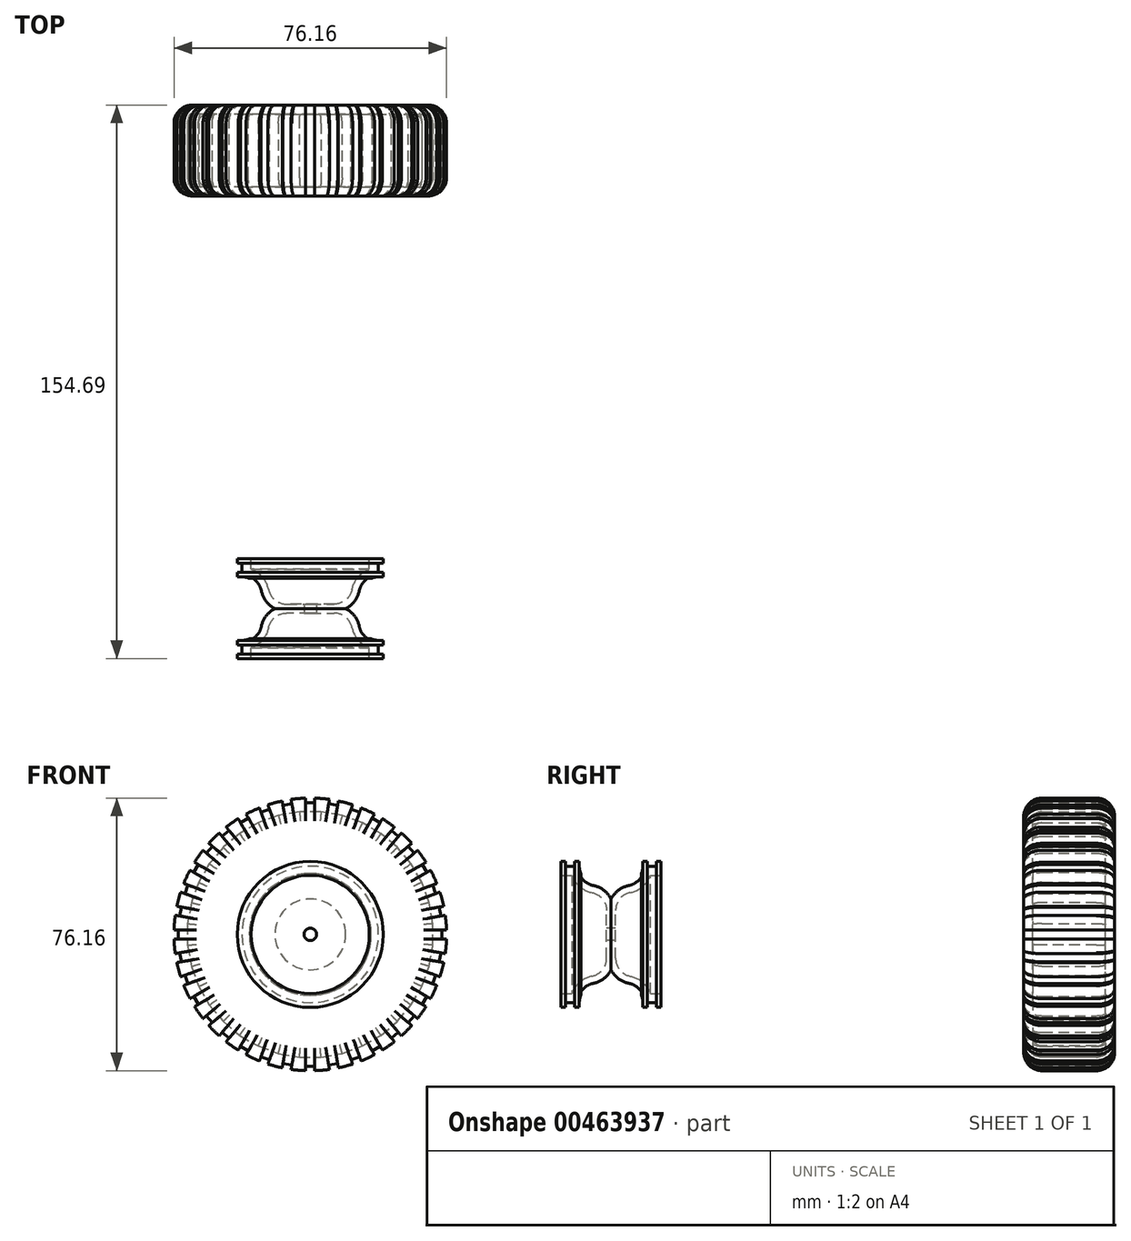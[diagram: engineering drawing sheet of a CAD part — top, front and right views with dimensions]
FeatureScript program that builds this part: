
annotation { "Feature Type Name" : "Feature", "Feature Type Description" : "" }
export const myFeature = defineFeature(function(context is Context, id is Id, definition is map)
    precondition{}
    {
        {
            var Q0;
            Q0=qCreatedBy(makeId("Front.planeOp"),FACE);
            var sketch = newSketch(context, id + "F0", { "sketchPlane" : qUnion([Q0])});
            skArc(sketch, "E0", {"start": v(-1.27, 38.08) * mm, "mid": v(-3.32, 37.96) * mm, "end": v(-5.36, 37.72) * mm});
            skCircle(sketch, "E1", {"center": v(0, 0) * mm, "radius": 19.05 * mm});
            skLineSegment(sketch, "E2.bottom", {"start": v(1.27, 36.83) * mm, "end": v(-1.27, 36.83) * mm});
            skLineSegment(sketch, "E2.left", {"start": v(1.27, 36.83) * mm, "end": v(1.27, 38.08) * mm});
            skLineSegment(sketch, "E2.right", {"start": v(-1.27, 36.83) * mm, "end": v(-1.27, 38.08) * mm});
            skPoint(sketch, "E2.middle", {"position": v(0, 38.1) * mm});
            skPoint(sketch, "E3.orphan", {"position": v(-1.27, 39.37) * mm});
            skPoint(sketch, "E4.orphan", {"position": v(1.27, 39.37) * mm});
            skPoint(sketch, "E5.1.0", {"position": v(8.09, 38.55) * mm});
            skPoint(sketch, "E5.1.1", {"position": v(5.59, 39) * mm});
            skPoint(sketch, "E5.1.2", {"position": v(6.62, 37.52) * mm});
            skLineSegment(sketch, "E5.1.3", {"start": v(5.14, 36.5) * mm, "end": v(5.36, 37.72) * mm});
            skLineSegment(sketch, "E5.1.4", {"start": v(7.65, 36.05) * mm, "end": v(7.86, 37.28) * mm});
            skLineSegment(sketch, "E5.1.5", {"start": v(7.65, 36.05) * mm, "end": v(5.14, 36.5) * mm});
            skPoint(sketch, "E5.2.0", {"position": v(14.66, 36.56) * mm});
            skPoint(sketch, "E5.2.1", {"position": v(12.27, 37.43) * mm});
            skPoint(sketch, "E5.2.2", {"position": v(13.03, 35.8) * mm});
            skLineSegment(sketch, "E5.2.3", {"start": v(11.4, 35.04) * mm, "end": v(11.83, 36.22) * mm});
            skLineSegment(sketch, "E5.2.4", {"start": v(13.8, 34.17) * mm, "end": v(14.22, 35.35) * mm});
            skLineSegment(sketch, "E5.2.5", {"start": v(13.8, 34.17) * mm, "end": v(11.4, 35.04) * mm});
            skPoint(sketch, "E5.3.0", {"position": v(20.78, 33.46) * mm});
            skPoint(sketch, "E5.3.1", {"position": v(18.59, 34.73) * mm});
            skPoint(sketch, "E5.3.2", {"position": v(19.05, 33) * mm});
            skLineSegment(sketch, "E5.3.3", {"start": v(17.32, 32.53) * mm, "end": v(17.94, 33.61) * mm});
            skLineSegment(sketch, "E5.3.4", {"start": v(19.51, 31.26) * mm, "end": v(20.14, 32.34) * mm});
            skLineSegment(sketch, "E5.3.5", {"start": v(19.51, 31.26) * mm, "end": v(17.32, 32.53) * mm});
            skPoint(sketch, "E5.4.0", {"position": v(26.28, 29.34) * mm});
            skPoint(sketch, "E5.4.1", {"position": v(24.33, 30.98) * mm});
            skPoint(sketch, "E5.4.2", {"position": v(24.5, 29.19) * mm});
            skLineSegment(sketch, "E5.4.3", {"start": v(22.7, 29.03) * mm, "end": v(23.5, 29.99) * mm});
            skLineSegment(sketch, "E5.4.4", {"start": v(24.65, 27.4) * mm, "end": v(25.45, 28.35) * mm});
            skLineSegment(sketch, "E5.4.5", {"start": v(24.65, 27.4) * mm, "end": v(22.7, 29.03) * mm});
            skPoint(sketch, "E5.5.0", {"position": v(30.98, 24.33) * mm});
            skPoint(sketch, "E5.5.1", {"position": v(29.34, 26.28) * mm});
            skPoint(sketch, "E5.5.2", {"position": v(29.19, 24.5) * mm});
            skLineSegment(sketch, "E5.5.3", {"start": v(27.4, 24.65) * mm, "end": v(28.35, 25.45) * mm});
            skLineSegment(sketch, "E5.5.4", {"start": v(29.03, 22.7) * mm, "end": v(29.99, 23.5) * mm});
            skLineSegment(sketch, "E5.5.5", {"start": v(29.03, 22.7) * mm, "end": v(27.4, 24.65) * mm});
            skPoint(sketch, "E5.6.0", {"position": v(34.73, 18.59) * mm});
            skPoint(sketch, "E5.6.1", {"position": v(33.46, 20.78) * mm});
            skPoint(sketch, "E5.6.2", {"position": v(33, 19.05) * mm});
            skLineSegment(sketch, "E5.6.3", {"start": v(31.26, 19.51) * mm, "end": v(32.34, 20.14) * mm});
            skLineSegment(sketch, "E5.6.4", {"start": v(32.53, 17.32) * mm, "end": v(33.61, 17.94) * mm});
            skLineSegment(sketch, "E5.6.5", {"start": v(32.53, 17.32) * mm, "end": v(31.26, 19.51) * mm});
            skPoint(sketch, "E5.7.0", {"position": v(37.43, 12.27) * mm});
            skPoint(sketch, "E5.7.1", {"position": v(36.56, 14.66) * mm});
            skPoint(sketch, "E5.7.2", {"position": v(35.8, 13.03) * mm});
            skLineSegment(sketch, "E5.7.3", {"start": v(34.17, 13.8) * mm, "end": v(35.35, 14.22) * mm});
            skLineSegment(sketch, "E5.7.4", {"start": v(35.04, 11.4) * mm, "end": v(36.22, 11.83) * mm});
            skLineSegment(sketch, "E5.7.5", {"start": v(35.04, 11.4) * mm, "end": v(34.17, 13.8) * mm});
            skPoint(sketch, "E5.8.0", {"position": v(39, 5.59) * mm});
            skPoint(sketch, "E5.8.1", {"position": v(38.55, 8.09) * mm});
            skPoint(sketch, "E5.8.2", {"position": v(37.52, 6.62) * mm});
            skLineSegment(sketch, "E5.8.3", {"start": v(36.05, 7.65) * mm, "end": v(37.28, 7.86) * mm});
            skLineSegment(sketch, "E5.8.4", {"start": v(36.5, 5.14) * mm, "end": v(37.72, 5.36) * mm});
            skLineSegment(sketch, "E5.8.5", {"start": v(36.5, 5.14) * mm, "end": v(36.05, 7.65) * mm});
            skPoint(sketch, "E5.9.0", {"position": v(39.37, -1.27) * mm});
            skPoint(sketch, "E5.9.1", {"position": v(39.37, 1.27) * mm});
            skPoint(sketch, "E5.9.2", {"position": v(38.1, 0) * mm});
            skLineSegment(sketch, "E5.9.3", {"start": v(36.83, 1.27) * mm, "end": v(38.08, 1.27) * mm});
            skLineSegment(sketch, "E5.9.4", {"start": v(36.83, -1.27) * mm, "end": v(38.08, -1.27) * mm});
            skLineSegment(sketch, "E5.9.5", {"start": v(36.83, -1.27) * mm, "end": v(36.83, 1.27) * mm});
            skPoint(sketch, "E5.10.0", {"position": v(38.55, -8.09) * mm});
            skPoint(sketch, "E5.10.1", {"position": v(39, -5.59) * mm});
            skPoint(sketch, "E5.10.2", {"position": v(37.52, -6.62) * mm});
            skLineSegment(sketch, "E5.10.3", {"start": v(36.5, -5.14) * mm, "end": v(37.72, -5.36) * mm});
            skLineSegment(sketch, "E5.10.4", {"start": v(36.05, -7.65) * mm, "end": v(37.28, -7.86) * mm});
            skLineSegment(sketch, "E5.10.5", {"start": v(36.05, -7.65) * mm, "end": v(36.5, -5.14) * mm});
            skPoint(sketch, "E5.11.0", {"position": v(36.56, -14.66) * mm});
            skPoint(sketch, "E5.11.1", {"position": v(37.43, -12.27) * mm});
            skPoint(sketch, "E5.11.2", {"position": v(35.8, -13.03) * mm});
            skLineSegment(sketch, "E5.11.3", {"start": v(35.04, -11.4) * mm, "end": v(36.22, -11.83) * mm});
            skLineSegment(sketch, "E5.11.4", {"start": v(34.17, -13.8) * mm, "end": v(35.35, -14.22) * mm});
            skLineSegment(sketch, "E5.11.5", {"start": v(34.17, -13.8) * mm, "end": v(35.04, -11.4) * mm});
            skPoint(sketch, "E5.12.0", {"position": v(33.46, -20.78) * mm});
            skPoint(sketch, "E5.12.1", {"position": v(34.73, -18.59) * mm});
            skPoint(sketch, "E5.12.2", {"position": v(33, -19.05) * mm});
            skLineSegment(sketch, "E5.12.3", {"start": v(32.53, -17.32) * mm, "end": v(33.61, -17.94) * mm});
            skLineSegment(sketch, "E5.12.4", {"start": v(31.26, -19.51) * mm, "end": v(32.34, -20.14) * mm});
            skLineSegment(sketch, "E5.12.5", {"start": v(31.26, -19.51) * mm, "end": v(32.53, -17.32) * mm});
            skPoint(sketch, "E5.13.0", {"position": v(29.34, -26.28) * mm});
            skPoint(sketch, "E5.13.1", {"position": v(30.98, -24.33) * mm});
            skPoint(sketch, "E5.13.2", {"position": v(29.19, -24.5) * mm});
            skLineSegment(sketch, "E5.13.3", {"start": v(29.03, -22.7) * mm, "end": v(29.99, -23.5) * mm});
            skLineSegment(sketch, "E5.13.4", {"start": v(27.4, -24.65) * mm, "end": v(28.35, -25.45) * mm});
            skLineSegment(sketch, "E5.13.5", {"start": v(27.4, -24.65) * mm, "end": v(29.03, -22.7) * mm});
            skPoint(sketch, "E5.14.0", {"position": v(24.33, -30.98) * mm});
            skPoint(sketch, "E5.14.1", {"position": v(26.28, -29.34) * mm});
            skPoint(sketch, "E5.14.2", {"position": v(24.5, -29.19) * mm});
            skLineSegment(sketch, "E5.14.3", {"start": v(24.65, -27.4) * mm, "end": v(25.45, -28.35) * mm});
            skLineSegment(sketch, "E5.14.4", {"start": v(22.7, -29.03) * mm, "end": v(23.5, -29.99) * mm});
            skLineSegment(sketch, "E5.14.5", {"start": v(22.7, -29.03) * mm, "end": v(24.65, -27.4) * mm});
            skPoint(sketch, "E5.15.0", {"position": v(18.59, -34.73) * mm});
            skPoint(sketch, "E5.15.1", {"position": v(20.78, -33.46) * mm});
            skPoint(sketch, "E5.15.2", {"position": v(19.05, -33) * mm});
            skLineSegment(sketch, "E5.15.3", {"start": v(19.51, -31.26) * mm, "end": v(20.14, -32.34) * mm});
            skLineSegment(sketch, "E5.15.4", {"start": v(17.32, -32.53) * mm, "end": v(17.94, -33.61) * mm});
            skLineSegment(sketch, "E5.15.5", {"start": v(17.32, -32.53) * mm, "end": v(19.51, -31.26) * mm});
            skPoint(sketch, "E5.16.0", {"position": v(12.27, -37.43) * mm});
            skPoint(sketch, "E5.16.1", {"position": v(14.66, -36.56) * mm});
            skPoint(sketch, "E5.16.2", {"position": v(13.03, -35.8) * mm});
            skLineSegment(sketch, "E5.16.3", {"start": v(13.8, -34.17) * mm, "end": v(14.22, -35.35) * mm});
            skLineSegment(sketch, "E5.16.4", {"start": v(11.4, -35.04) * mm, "end": v(11.83, -36.22) * mm});
            skLineSegment(sketch, "E5.16.5", {"start": v(11.4, -35.04) * mm, "end": v(13.8, -34.17) * mm});
            skPoint(sketch, "E5.17.0", {"position": v(5.59, -39) * mm});
            skPoint(sketch, "E5.17.1", {"position": v(8.09, -38.55) * mm});
            skPoint(sketch, "E5.17.2", {"position": v(6.62, -37.52) * mm});
            skLineSegment(sketch, "E5.17.3", {"start": v(7.65, -36.05) * mm, "end": v(7.86, -37.28) * mm});
            skLineSegment(sketch, "E5.17.4", {"start": v(5.14, -36.5) * mm, "end": v(5.36, -37.72) * mm});
            skLineSegment(sketch, "E5.17.5", {"start": v(5.14, -36.5) * mm, "end": v(7.65, -36.05) * mm});
            skPoint(sketch, "E5.18.0", {"position": v(-1.27, -39.37) * mm});
            skPoint(sketch, "E5.18.1", {"position": v(1.27, -39.37) * mm});
            skPoint(sketch, "E5.18.2", {"position": v(0, -38.1) * mm});
            skLineSegment(sketch, "E5.18.3", {"start": v(1.27, -36.83) * mm, "end": v(1.27, -38.08) * mm});
            skLineSegment(sketch, "E5.18.4", {"start": v(-1.27, -36.83) * mm, "end": v(-1.27, -38.08) * mm});
            skLineSegment(sketch, "E5.18.5", {"start": v(-1.27, -36.83) * mm, "end": v(1.27, -36.83) * mm});
            skPoint(sketch, "E5.19.0", {"position": v(-8.09, -38.55) * mm});
            skPoint(sketch, "E5.19.1", {"position": v(-5.59, -39) * mm});
            skPoint(sketch, "E5.19.2", {"position": v(-6.62, -37.52) * mm});
            skLineSegment(sketch, "E5.19.3", {"start": v(-5.14, -36.5) * mm, "end": v(-5.36, -37.72) * mm});
            skLineSegment(sketch, "E5.19.4", {"start": v(-7.65, -36.05) * mm, "end": v(-7.86, -37.28) * mm});
            skLineSegment(sketch, "E5.19.5", {"start": v(-7.65, -36.05) * mm, "end": v(-5.14, -36.5) * mm});
            skPoint(sketch, "E5.20.0", {"position": v(-14.66, -36.56) * mm});
            skPoint(sketch, "E5.20.1", {"position": v(-12.27, -37.43) * mm});
            skPoint(sketch, "E5.20.2", {"position": v(-13.03, -35.8) * mm});
            skLineSegment(sketch, "E5.20.3", {"start": v(-11.4, -35.04) * mm, "end": v(-11.83, -36.22) * mm});
            skLineSegment(sketch, "E5.20.4", {"start": v(-13.8, -34.17) * mm, "end": v(-14.22, -35.35) * mm});
            skLineSegment(sketch, "E5.20.5", {"start": v(-13.8, -34.17) * mm, "end": v(-11.4, -35.04) * mm});
            skPoint(sketch, "E5.21.0", {"position": v(-20.78, -33.46) * mm});
            skPoint(sketch, "E5.21.1", {"position": v(-18.59, -34.73) * mm});
            skPoint(sketch, "E5.21.2", {"position": v(-19.05, -33) * mm});
            skLineSegment(sketch, "E5.21.3", {"start": v(-17.32, -32.53) * mm, "end": v(-17.94, -33.61) * mm});
            skLineSegment(sketch, "E5.21.4", {"start": v(-19.51, -31.26) * mm, "end": v(-20.14, -32.34) * mm});
            skLineSegment(sketch, "E5.21.5", {"start": v(-19.51, -31.26) * mm, "end": v(-17.32, -32.53) * mm});
            skPoint(sketch, "E5.22.0", {"position": v(-26.28, -29.34) * mm});
            skPoint(sketch, "E5.22.1", {"position": v(-24.33, -30.98) * mm});
            skPoint(sketch, "E5.22.2", {"position": v(-24.5, -29.19) * mm});
            skLineSegment(sketch, "E5.22.3", {"start": v(-22.7, -29.03) * mm, "end": v(-23.5, -29.99) * mm});
            skLineSegment(sketch, "E5.22.4", {"start": v(-24.65, -27.4) * mm, "end": v(-25.45, -28.35) * mm});
            skLineSegment(sketch, "E5.22.5", {"start": v(-24.65, -27.4) * mm, "end": v(-22.7, -29.03) * mm});
            skPoint(sketch, "E5.23.0", {"position": v(-30.98, -24.33) * mm});
            skPoint(sketch, "E5.23.1", {"position": v(-29.34, -26.28) * mm});
            skPoint(sketch, "E5.23.2", {"position": v(-29.19, -24.5) * mm});
            skLineSegment(sketch, "E5.23.3", {"start": v(-27.4, -24.65) * mm, "end": v(-28.35, -25.45) * mm});
            skLineSegment(sketch, "E5.23.4", {"start": v(-29.03, -22.7) * mm, "end": v(-29.99, -23.5) * mm});
            skLineSegment(sketch, "E5.23.5", {"start": v(-29.03, -22.7) * mm, "end": v(-27.4, -24.65) * mm});
            skPoint(sketch, "E5.24.0", {"position": v(-34.73, -18.59) * mm});
            skPoint(sketch, "E5.24.1", {"position": v(-33.46, -20.78) * mm});
            skPoint(sketch, "E5.24.2", {"position": v(-33, -19.05) * mm});
            skLineSegment(sketch, "E5.24.3", {"start": v(-31.26, -19.51) * mm, "end": v(-32.34, -20.14) * mm});
            skLineSegment(sketch, "E5.24.4", {"start": v(-32.53, -17.32) * mm, "end": v(-33.61, -17.94) * mm});
            skLineSegment(sketch, "E5.24.5", {"start": v(-32.53, -17.32) * mm, "end": v(-31.26, -19.51) * mm});
            skPoint(sketch, "E5.25.0", {"position": v(-37.43, -12.27) * mm});
            skPoint(sketch, "E5.25.1", {"position": v(-36.56, -14.66) * mm});
            skPoint(sketch, "E5.25.2", {"position": v(-35.8, -13.03) * mm});
            skLineSegment(sketch, "E5.25.3", {"start": v(-34.17, -13.8) * mm, "end": v(-35.35, -14.22) * mm});
            skLineSegment(sketch, "E5.25.4", {"start": v(-35.04, -11.4) * mm, "end": v(-36.22, -11.83) * mm});
            skLineSegment(sketch, "E5.25.5", {"start": v(-35.04, -11.4) * mm, "end": v(-34.17, -13.8) * mm});
            skPoint(sketch, "E5.26.0", {"position": v(-39, -5.59) * mm});
            skPoint(sketch, "E5.26.1", {"position": v(-38.55, -8.09) * mm});
            skPoint(sketch, "E5.26.2", {"position": v(-37.52, -6.62) * mm});
            skLineSegment(sketch, "E5.26.3", {"start": v(-36.05, -7.65) * mm, "end": v(-37.28, -7.86) * mm});
            skLineSegment(sketch, "E5.26.4", {"start": v(-36.5, -5.14) * mm, "end": v(-37.72, -5.36) * mm});
            skLineSegment(sketch, "E5.26.5", {"start": v(-36.5, -5.14) * mm, "end": v(-36.05, -7.65) * mm});
            skPoint(sketch, "E5.27.0", {"position": v(-39.37, 1.27) * mm});
            skPoint(sketch, "E5.27.1", {"position": v(-39.37, -1.27) * mm});
            skPoint(sketch, "E5.27.2", {"position": v(-38.1, 0) * mm});
            skLineSegment(sketch, "E5.27.3", {"start": v(-36.83, -1.27) * mm, "end": v(-38.08, -1.27) * mm});
            skLineSegment(sketch, "E5.27.4", {"start": v(-36.83, 1.27) * mm, "end": v(-38.08, 1.27) * mm});
            skLineSegment(sketch, "E5.27.5", {"start": v(-36.83, 1.27) * mm, "end": v(-36.83, -1.27) * mm});
            skPoint(sketch, "E5.28.0", {"position": v(-38.55, 8.09) * mm});
            skPoint(sketch, "E5.28.1", {"position": v(-39, 5.59) * mm});
            skPoint(sketch, "E5.28.2", {"position": v(-37.52, 6.62) * mm});
            skLineSegment(sketch, "E5.28.3", {"start": v(-36.5, 5.14) * mm, "end": v(-37.72, 5.36) * mm});
            skLineSegment(sketch, "E5.28.4", {"start": v(-36.05, 7.65) * mm, "end": v(-37.28, 7.86) * mm});
            skLineSegment(sketch, "E5.28.5", {"start": v(-36.05, 7.65) * mm, "end": v(-36.5, 5.14) * mm});
            skPoint(sketch, "E5.29.0", {"position": v(-36.56, 14.66) * mm});
            skPoint(sketch, "E5.29.1", {"position": v(-37.43, 12.27) * mm});
            skPoint(sketch, "E5.29.2", {"position": v(-35.8, 13.03) * mm});
            skLineSegment(sketch, "E5.29.3", {"start": v(-35.04, 11.4) * mm, "end": v(-36.22, 11.83) * mm});
            skLineSegment(sketch, "E5.29.4", {"start": v(-34.17, 13.8) * mm, "end": v(-35.35, 14.22) * mm});
            skLineSegment(sketch, "E5.29.5", {"start": v(-34.17, 13.8) * mm, "end": v(-35.04, 11.4) * mm});
            skPoint(sketch, "E5.30.0", {"position": v(-33.46, 20.78) * mm});
            skPoint(sketch, "E5.30.1", {"position": v(-34.73, 18.59) * mm});
            skPoint(sketch, "E5.30.2", {"position": v(-33, 19.05) * mm});
            skLineSegment(sketch, "E5.30.3", {"start": v(-32.53, 17.32) * mm, "end": v(-33.61, 17.94) * mm});
            skLineSegment(sketch, "E5.30.4", {"start": v(-31.26, 19.51) * mm, "end": v(-32.34, 20.14) * mm});
            skLineSegment(sketch, "E5.30.5", {"start": v(-31.26, 19.51) * mm, "end": v(-32.53, 17.32) * mm});
            skPoint(sketch, "E5.31.0", {"position": v(-29.34, 26.28) * mm});
            skPoint(sketch, "E5.31.1", {"position": v(-30.98, 24.33) * mm});
            skPoint(sketch, "E5.31.2", {"position": v(-29.19, 24.5) * mm});
            skLineSegment(sketch, "E5.31.3", {"start": v(-29.03, 22.7) * mm, "end": v(-29.99, 23.5) * mm});
            skLineSegment(sketch, "E5.31.4", {"start": v(-27.4, 24.65) * mm, "end": v(-28.35, 25.45) * mm});
            skLineSegment(sketch, "E5.31.5", {"start": v(-27.4, 24.65) * mm, "end": v(-29.03, 22.7) * mm});
            skPoint(sketch, "E5.32.0", {"position": v(-24.33, 30.98) * mm});
            skPoint(sketch, "E5.32.1", {"position": v(-26.28, 29.34) * mm});
            skPoint(sketch, "E5.32.2", {"position": v(-24.5, 29.19) * mm});
            skLineSegment(sketch, "E5.32.3", {"start": v(-24.65, 27.4) * mm, "end": v(-25.45, 28.35) * mm});
            skLineSegment(sketch, "E5.32.4", {"start": v(-22.7, 29.03) * mm, "end": v(-23.5, 29.99) * mm});
            skLineSegment(sketch, "E5.32.5", {"start": v(-22.7, 29.03) * mm, "end": v(-24.65, 27.4) * mm});
            skPoint(sketch, "E5.33.0", {"position": v(-18.59, 34.73) * mm});
            skPoint(sketch, "E5.33.1", {"position": v(-20.78, 33.46) * mm});
            skPoint(sketch, "E5.33.2", {"position": v(-19.05, 33) * mm});
            skLineSegment(sketch, "E5.33.3", {"start": v(-19.51, 31.26) * mm, "end": v(-20.14, 32.34) * mm});
            skLineSegment(sketch, "E5.33.4", {"start": v(-17.32, 32.53) * mm, "end": v(-17.94, 33.61) * mm});
            skLineSegment(sketch, "E5.33.5", {"start": v(-17.32, 32.53) * mm, "end": v(-19.51, 31.26) * mm});
            skPoint(sketch, "E5.34.0", {"position": v(-12.27, 37.43) * mm});
            skPoint(sketch, "E5.34.1", {"position": v(-14.66, 36.56) * mm});
            skPoint(sketch, "E5.34.2", {"position": v(-13.03, 35.8) * mm});
            skLineSegment(sketch, "E5.34.3", {"start": v(-13.8, 34.17) * mm, "end": v(-14.22, 35.35) * mm});
            skLineSegment(sketch, "E5.34.4", {"start": v(-11.4, 35.04) * mm, "end": v(-11.83, 36.22) * mm});
            skLineSegment(sketch, "E5.34.5", {"start": v(-11.4, 35.04) * mm, "end": v(-13.8, 34.17) * mm});
            skPoint(sketch, "E5.35.0", {"position": v(-5.59, 39) * mm});
            skPoint(sketch, "E5.35.1", {"position": v(-8.09, 38.55) * mm});
            skPoint(sketch, "E5.35.2", {"position": v(-6.62, 37.52) * mm});
            skLineSegment(sketch, "E5.35.3", {"start": v(-7.65, 36.05) * mm, "end": v(-7.86, 37.28) * mm});
            skLineSegment(sketch, "E5.35.4", {"start": v(-5.14, 36.5) * mm, "end": v(-5.36, 37.72) * mm});
            skLineSegment(sketch, "E5.35.5", {"start": v(-5.14, 36.5) * mm, "end": v(-7.65, 36.05) * mm});
            skLineSegment(sketch, "E5.anchor1", {"start": v(0, 0) * mm, "end": v(-1.27, 36.83) * mm, "construction": true});
            skLineSegment(sketch, "E5.anchor2", {"start": v(0, 0) * mm, "end": v(-7.65, 36.05) * mm, "construction": true});
            skArc(sketch, "E6.trimOffspring", {"start": v(-7.86, 37.28) * mm, "mid": v(-9.86, 36.8) * mm, "end": v(-11.83, 36.22) * mm});
            skArc(sketch, "E7.trimOffspring", {"start": v(-14.22, 35.35) * mm, "mid": v(-16.1, 34.53) * mm, "end": v(-17.94, 33.61) * mm});
            skArc(sketch, "E8.trimOffspring", {"start": v(-20.14, 32.34) * mm, "mid": v(-21.85, 31.2) * mm, "end": v(-23.5, 29.99) * mm});
            skArc(sketch, "E9.trimOffspring", {"start": v(-25.45, 28.35) * mm, "mid": v(-26.94, 26.94) * mm, "end": v(-28.35, 25.45) * mm});
            skArc(sketch, "E10.trimOffspring", {"start": v(5.36, 37.72) * mm, "mid": v(3.32, 37.96) * mm, "end": v(1.27, 38.08) * mm});
            skArc(sketch, "E11.trimOffspring", {"start": v(11.83, 36.22) * mm, "mid": v(9.86, 36.8) * mm, "end": v(7.86, 37.28) * mm});
            skArc(sketch, "E12.trimOffspring", {"start": v(17.94, 33.61) * mm, "mid": v(16.1, 34.53) * mm, "end": v(14.22, 35.35) * mm});
            skArc(sketch, "E13.trimOffspring", {"start": v(23.5, 29.99) * mm, "mid": v(21.85, 31.2) * mm, "end": v(20.14, 32.34) * mm});
            skArc(sketch, "E14.trimOffspring", {"start": v(28.35, 25.45) * mm, "mid": v(26.94, 26.94) * mm, "end": v(25.45, 28.35) * mm});
            skArc(sketch, "E15.trimOffspring", {"start": v(32.34, 20.14) * mm, "mid": v(31.2, 21.85) * mm, "end": v(29.99, 23.5) * mm});
            skArc(sketch, "E16.trimOffspring", {"start": v(35.35, 14.22) * mm, "mid": v(34.53, 16.1) * mm, "end": v(33.61, 17.94) * mm});
            skArc(sketch, "E17.trimOffspring", {"start": v(37.28, 7.86) * mm, "mid": v(36.8, 9.86) * mm, "end": v(36.22, 11.83) * mm});
            skArc(sketch, "E18.trimOffspring", {"start": v(38.08, 1.27) * mm, "mid": v(37.96, 3.32) * mm, "end": v(37.72, 5.36) * mm});
            skArc(sketch, "E19.trimOffspring", {"start": v(37.72, -5.36) * mm, "mid": v(37.96, -3.32) * mm, "end": v(38.08, -1.27) * mm});
            skArc(sketch, "E20.trimOffspring", {"start": v(36.22, -11.83) * mm, "mid": v(36.8, -9.86) * mm, "end": v(37.28, -7.86) * mm});
            skArc(sketch, "E21.trimOffspring", {"start": v(33.61, -17.94) * mm, "mid": v(34.53, -16.1) * mm, "end": v(35.35, -14.22) * mm});
            skArc(sketch, "E22.trimOffspring", {"start": v(29.99, -23.5) * mm, "mid": v(31.2, -21.85) * mm, "end": v(32.34, -20.14) * mm});
            skArc(sketch, "E23.trimOffspring", {"start": v(25.45, -28.35) * mm, "mid": v(26.94, -26.94) * mm, "end": v(28.35, -25.45) * mm});
            skArc(sketch, "E24.trimOffspring", {"start": v(20.14, -32.34) * mm, "mid": v(21.85, -31.2) * mm, "end": v(23.5, -29.99) * mm});
            skArc(sketch, "E25.trimOffspring", {"start": v(14.22, -35.35) * mm, "mid": v(16.1, -34.53) * mm, "end": v(17.94, -33.61) * mm});
            skArc(sketch, "E26.trimOffspring", {"start": v(7.86, -37.28) * mm, "mid": v(9.86, -36.8) * mm, "end": v(11.83, -36.22) * mm});
            skArc(sketch, "E27.trimOffspring", {"start": v(1.27, -38.08) * mm, "mid": v(3.32, -37.96) * mm, "end": v(5.36, -37.72) * mm});
            skArc(sketch, "E28.trimOffspring", {"start": v(-5.36, -37.72) * mm, "mid": v(-3.32, -37.96) * mm, "end": v(-1.27, -38.08) * mm});
            skArc(sketch, "E29.trimOffspring", {"start": v(-11.83, -36.22) * mm, "mid": v(-9.86, -36.8) * mm, "end": v(-7.86, -37.28) * mm});
            skArc(sketch, "E30.trimOffspring", {"start": v(-17.94, -33.61) * mm, "mid": v(-16.1, -34.53) * mm, "end": v(-14.22, -35.35) * mm});
            skArc(sketch, "E31.trimOffspring", {"start": v(-23.5, -29.99) * mm, "mid": v(-21.85, -31.2) * mm, "end": v(-20.14, -32.34) * mm});
            skArc(sketch, "E32.trimOffspring", {"start": v(-28.35, -25.45) * mm, "mid": v(-26.94, -26.94) * mm, "end": v(-25.45, -28.35) * mm});
            skArc(sketch, "E33.trimOffspring", {"start": v(-32.34, -20.14) * mm, "mid": v(-31.2, -21.85) * mm, "end": v(-29.99, -23.5) * mm});
            skArc(sketch, "E34.trimOffspring", {"start": v(-35.35, -14.22) * mm, "mid": v(-34.53, -16.1) * mm, "end": v(-33.61, -17.94) * mm});
            skArc(sketch, "E35.trimOffspring", {"start": v(-37.28, -7.86) * mm, "mid": v(-36.8, -9.86) * mm, "end": v(-36.22, -11.83) * mm});
            skArc(sketch, "E36.trimOffspring", {"start": v(-38.08, -1.27) * mm, "mid": v(-37.96, -3.32) * mm, "end": v(-37.72, -5.36) * mm});
            skArc(sketch, "E37.trimOffspring", {"start": v(-37.72, 5.36) * mm, "mid": v(-37.96, 3.32) * mm, "end": v(-38.08, 1.27) * mm});
            skArc(sketch, "E38.trimOffspring", {"start": v(-36.22, 11.83) * mm, "mid": v(-36.8, 9.86) * mm, "end": v(-37.28, 7.86) * mm});
            skArc(sketch, "E39.trimOffspring", {"start": v(-33.61, 17.94) * mm, "mid": v(-34.53, 16.1) * mm, "end": v(-35.35, 14.22) * mm});
            skArc(sketch, "E40.trimOffspring", {"start": v(-29.99, 23.5) * mm, "mid": v(-31.2, 21.85) * mm, "end": v(-32.34, 20.14) * mm});
            skSolve(sketch);
        }
        {
            var Q0;
            Q0 = qSketchRegion(id + "F0", true);
            extrude(context, id + "F1", {"entities" : qUnion([Q0]), "depth" : 25.4 * mm, "symmetric" : true});
        }
        {
            var Q0;
            Q0=makeQuery(id+"F1.opExtrude","CAP_EDGE",EDGE,{"disambiguationData":[OSD([sQuery(id+"F0.wireOp",EDGE,"E5.1.5")])],"isStart":false});
            var Q1;
            Q1=makeQuery(id+"F1.opExtrude","CAP_EDGE",EDGE,{"disambiguationData":[OSD([sQuery(id+"F0.wireOp",EDGE,"E5.2.5")])],"isStart":false});
            var Q2;
            Q2=makeQuery(id+"F1.opExtrude","CAP_EDGE",EDGE,{"disambiguationData":[OSD([sQuery(id+"F0.wireOp",EDGE,"E5.3.5")])],"isStart":false});
            var Q3;
            Q3=makeQuery(id+"F1.opExtrude","CAP_EDGE",EDGE,{"disambiguationData":[OSD([sQuery(id+"F0.wireOp",EDGE,"E2.bottom")])],"isStart":false});
            var Q4;
            Q4=makeQuery(id+"F1.opExtrude","CAP_EDGE",EDGE,{"disambiguationData":[OSD([sQuery(id+"F0.wireOp",EDGE,"E5.35.5")])],"isStart":false});
            var Q5;
            Q5=makeQuery(id+"F1.opExtrude","CAP_EDGE",EDGE,{"disambiguationData":[OSD([sQuery(id+"F0.wireOp",EDGE,"E5.34.5")])],"isStart":false});
            var Q6;
            Q6=makeQuery(id+"F1.opExtrude","CAP_EDGE",EDGE,{"disambiguationData":[OSD([sQuery(id+"F0.wireOp",EDGE,"E5.4.5")])],"isStart":false});
            var Q7;
            Q7=makeQuery(id+"F1.opExtrude","CAP_EDGE",EDGE,{"disambiguationData":[OSD([sQuery(id+"F0.wireOp",EDGE,"E5.5.5")])],"isStart":false});
            var Q8;
            Q8=makeQuery(id+"F1.opExtrude","CAP_EDGE",EDGE,{"disambiguationData":[OSD([sQuery(id+"F0.wireOp",EDGE,"E5.6.5")])],"isStart":false});
            var Q9;
            Q9=makeQuery(id+"F1.opExtrude","CAP_EDGE",EDGE,{"disambiguationData":[OSD([sQuery(id+"F0.wireOp",EDGE,"E5.7.5")])],"isStart":false});
            var Q10;
            Q10=makeQuery(id+"F1.opExtrude","CAP_EDGE",EDGE,{"disambiguationData":[OSD([sQuery(id+"F0.wireOp",EDGE,"E5.8.5")])],"isStart":false});
            var Q11;
            Q11=makeQuery(id+"F1.opExtrude","CAP_EDGE",EDGE,{"disambiguationData":[OSD([sQuery(id+"F0.wireOp",EDGE,"E5.9.5")])],"isStart":false});
            var Q12;
            Q12=makeQuery(id+"F1.opExtrude","CAP_EDGE",EDGE,{"disambiguationData":[OSD([sQuery(id+"F0.wireOp",EDGE,"E5.10.5")])],"isStart":false});
            var Q13;
            Q13=makeQuery(id+"F1.opExtrude","CAP_EDGE",EDGE,{"disambiguationData":[OSD([sQuery(id+"F0.wireOp",EDGE,"E5.11.5")])],"isStart":false});
            var Q14;
            Q14=makeQuery(id+"F1.opExtrude","CAP_EDGE",EDGE,{"disambiguationData":[OSD([sQuery(id+"F0.wireOp",EDGE,"E5.12.5")])],"isStart":false});
            var Q15;
            Q15=makeQuery(id+"F1.opExtrude","CAP_EDGE",EDGE,{"disambiguationData":[OSD([sQuery(id+"F0.wireOp",EDGE,"E5.13.5")])],"isStart":false});
            var Q16;
            Q16=makeQuery(id+"F1.opExtrude","CAP_EDGE",EDGE,{"disambiguationData":[OSD([sQuery(id+"F0.wireOp",EDGE,"E5.14.5")])],"isStart":false});
            var Q17;
            Q17=makeQuery(id+"F1.opExtrude","CAP_EDGE",EDGE,{"disambiguationData":[OSD([sQuery(id+"F0.wireOp",EDGE,"E5.15.5")])],"isStart":false});
            var Q18;
            Q18=makeQuery(id+"F1.opExtrude","CAP_EDGE",EDGE,{"disambiguationData":[OSD([sQuery(id+"F0.wireOp",EDGE,"E5.21.5")])],"isStart":false});
            var Q19;
            Q19=makeQuery(id+"F1.opExtrude","CAP_EDGE",EDGE,{"disambiguationData":[OSD([sQuery(id+"F0.wireOp",EDGE,"E5.20.5")])],"isStart":false});
            var Q20;
            Q20=makeQuery(id+"F1.opExtrude","CAP_EDGE",EDGE,{"disambiguationData":[OSD([sQuery(id+"F0.wireOp",EDGE,"E5.19.5")])],"isStart":false});
            var Q21;
            Q21=makeQuery(id+"F1.opExtrude","CAP_EDGE",EDGE,{"disambiguationData":[OSD([sQuery(id+"F0.wireOp",EDGE,"E5.18.5")])],"isStart":false});
            var Q22;
            Q22=makeQuery(id+"F1.opExtrude","CAP_EDGE",EDGE,{"disambiguationData":[OSD([sQuery(id+"F0.wireOp",EDGE,"E5.17.5")])],"isStart":false});
            var Q23;
            Q23=makeQuery(id+"F1.opExtrude","CAP_EDGE",EDGE,{"disambiguationData":[OSD([sQuery(id+"F0.wireOp",EDGE,"E5.16.5")])],"isStart":false});
            var Q24;
            Q24=makeQuery(id+"F1.opExtrude","CAP_EDGE",EDGE,{"disambiguationData":[OSD([sQuery(id+"F0.wireOp",EDGE,"E5.22.5")])],"isStart":false});
            var Q25;
            Q25=makeQuery(id+"F1.opExtrude","CAP_EDGE",EDGE,{"disambiguationData":[OSD([sQuery(id+"F0.wireOp",EDGE,"E5.23.5")])],"isStart":false});
            var Q26;
            Q26=makeQuery(id+"F1.opExtrude","CAP_EDGE",EDGE,{"disambiguationData":[OSD([sQuery(id+"F0.wireOp",EDGE,"E5.24.5")])],"isStart":false});
            var Q27;
            Q27=makeQuery(id+"F1.opExtrude","CAP_EDGE",EDGE,{"disambiguationData":[OSD([sQuery(id+"F0.wireOp",EDGE,"E5.25.5")])],"isStart":false});
            var Q28;
            Q28=makeQuery(id+"F1.opExtrude","CAP_EDGE",EDGE,{"disambiguationData":[OSD([sQuery(id+"F0.wireOp",EDGE,"E5.26.5")])],"isStart":false});
            var Q29;
            Q29=makeQuery(id+"F1.opExtrude","CAP_EDGE",EDGE,{"disambiguationData":[OSD([sQuery(id+"F0.wireOp",EDGE,"E5.27.5")])],"isStart":false});
            var Q30;
            Q30=makeQuery(id+"F1.opExtrude","CAP_EDGE",EDGE,{"disambiguationData":[OSD([sQuery(id+"F0.wireOp",EDGE,"E5.28.5")])],"isStart":false});
            var Q31;
            Q31=makeQuery(id+"F1.opExtrude","CAP_EDGE",EDGE,{"disambiguationData":[OSD([sQuery(id+"F0.wireOp",EDGE,"E5.29.5")])],"isStart":false});
            var Q32;
            Q32=makeQuery(id+"F1.opExtrude","CAP_EDGE",EDGE,{"disambiguationData":[OSD([sQuery(id+"F0.wireOp",EDGE,"E5.30.5")])],"isStart":false});
            var Q33;
            Q33=makeQuery(id+"F1.opExtrude","CAP_EDGE",EDGE,{"disambiguationData":[OSD([sQuery(id+"F0.wireOp",EDGE,"E5.31.5")])],"isStart":false});
            var Q34;
            Q34=makeQuery(id+"F1.opExtrude","CAP_EDGE",EDGE,{"disambiguationData":[OSD([sQuery(id+"F0.wireOp",EDGE,"E5.32.5")])],"isStart":false});
            var Q35;
            Q35=makeQuery(id+"F1.opExtrude","CAP_EDGE",EDGE,{"disambiguationData":[OSD([sQuery(id+"F0.wireOp",EDGE,"E5.33.5")])],"isStart":false});
            fillet(context, id + "F2", {"entities" : qUnion([Q0, Q1, Q2, Q3, Q4, Q5, Q6, Q7, Q8, Q9, Q10, Q11, Q12, Q13, Q14, Q15, Q16, Q17, Q18, Q19, Q20, Q21, Q22, Q23, Q24, Q25, Q26, Q27, Q28, Q29, Q30, Q31, Q32, Q33, Q34, Q35]), "radius" : 5.08 * mm, "tangentPropagation" : true, "allowEdgeOverflow" : false});
        }
        {
            var Q0;
            Q0=makeQuery(id+"F1.opExtrude","CAP_EDGE",EDGE,{"disambiguationData":[OSD([sQuery(id+"F0.wireOp",EDGE,"E2.bottom")])],"isStart":true});
            var Q1;
            Q1=makeQuery(id+"F1.opExtrude","CAP_EDGE",EDGE,{"disambiguationData":[OSD([sQuery(id+"F0.wireOp",EDGE,"E5.2.5")])],"isStart":true});
            var Q2;
            Q2=makeQuery(id+"F1.opExtrude","CAP_EDGE",EDGE,{"disambiguationData":[OSD([sQuery(id+"F0.wireOp",EDGE,"E5.1.5")])],"isStart":true});
            var Q3;
            Q3=makeQuery(id+"F1.opExtrude","CAP_EDGE",EDGE,{"disambiguationData":[OSD([sQuery(id+"F0.wireOp",EDGE,"E5.3.5")])],"isStart":true});
            var Q4;
            Q4=makeQuery(id+"F1.opExtrude","CAP_EDGE",EDGE,{"disambiguationData":[OSD([sQuery(id+"F0.wireOp",EDGE,"E5.4.5")])],"isStart":true});
            var Q5;
            Q5=makeQuery(id+"F1.opExtrude","CAP_EDGE",EDGE,{"disambiguationData":[OSD([sQuery(id+"F0.wireOp",EDGE,"E5.35.5")])],"isStart":true});
            var Q6;
            Q6=makeQuery(id+"F1.opExtrude","CAP_EDGE",EDGE,{"disambiguationData":[OSD([sQuery(id+"F0.wireOp",EDGE,"E5.34.5")])],"isStart":true});
            var Q7;
            Q7=makeQuery(id+"F1.opExtrude","CAP_EDGE",EDGE,{"disambiguationData":[OSD([sQuery(id+"F0.wireOp",EDGE,"E5.33.5")])],"isStart":true});
            var Q8;
            Q8=makeQuery(id+"F1.opExtrude","CAP_EDGE",EDGE,{"disambiguationData":[OSD([sQuery(id+"F0.wireOp",EDGE,"E5.32.5")])],"isStart":true});
            var Q9;
            Q9=makeQuery(id+"F1.opExtrude","CAP_EDGE",EDGE,{"disambiguationData":[OSD([sQuery(id+"F0.wireOp",EDGE,"E5.31.5")])],"isStart":true});
            var Q10;
            Q10=makeQuery(id+"F1.opExtrude","CAP_EDGE",EDGE,{"disambiguationData":[OSD([sQuery(id+"F0.wireOp",EDGE,"E5.30.5")])],"isStart":true});
            var Q11;
            Q11=makeQuery(id+"F1.opExtrude","CAP_EDGE",EDGE,{"disambiguationData":[OSD([sQuery(id+"F0.wireOp",EDGE,"E5.29.5")])],"isStart":true});
            var Q12;
            Q12=makeQuery(id+"F1.opExtrude","CAP_EDGE",EDGE,{"disambiguationData":[OSD([sQuery(id+"F0.wireOp",EDGE,"E5.28.5")])],"isStart":true});
            var Q13;
            Q13=makeQuery(id+"F1.opExtrude","CAP_EDGE",EDGE,{"disambiguationData":[OSD([sQuery(id+"F0.wireOp",EDGE,"E5.27.5")])],"isStart":true});
            var Q14;
            Q14=makeQuery(id+"F1.opExtrude","CAP_EDGE",EDGE,{"disambiguationData":[OSD([sQuery(id+"F0.wireOp",EDGE,"E5.26.5")])],"isStart":true});
            var Q15;
            Q15=makeQuery(id+"F1.opExtrude","CAP_EDGE",EDGE,{"disambiguationData":[OSD([sQuery(id+"F0.wireOp",EDGE,"E5.25.5")])],"isStart":true});
            var Q16;
            Q16=makeQuery(id+"F1.opExtrude","CAP_EDGE",EDGE,{"disambiguationData":[OSD([sQuery(id+"F0.wireOp",EDGE,"E5.24.5")])],"isStart":true});
            var Q17;
            Q17=makeQuery(id+"F1.opExtrude","CAP_EDGE",EDGE,{"disambiguationData":[OSD([sQuery(id+"F0.wireOp",EDGE,"E5.23.5")])],"isStart":true});
            var Q18;
            Q18=makeQuery(id+"F1.opExtrude","CAP_EDGE",EDGE,{"disambiguationData":[OSD([sQuery(id+"F0.wireOp",EDGE,"E5.22.5")])],"isStart":true});
            var Q19;
            Q19=makeQuery(id+"F1.opExtrude","CAP_EDGE",EDGE,{"disambiguationData":[OSD([sQuery(id+"F0.wireOp",EDGE,"E5.21.5")])],"isStart":true});
            var Q20;
            Q20=makeQuery(id+"F1.opExtrude","CAP_EDGE",EDGE,{"disambiguationData":[OSD([sQuery(id+"F0.wireOp",EDGE,"E5.19.5")])],"isStart":true});
            var Q21;
            Q21=makeQuery(id+"F1.opExtrude","CAP_EDGE",EDGE,{"disambiguationData":[OSD([sQuery(id+"F0.wireOp",EDGE,"E5.18.5")])],"isStart":true});
            var Q22;
            Q22=makeQuery(id+"F1.opExtrude","CAP_EDGE",EDGE,{"disambiguationData":[OSD([sQuery(id+"F0.wireOp",EDGE,"E5.17.5")])],"isStart":true});
            var Q23;
            Q23=makeQuery(id+"F1.opExtrude","CAP_EDGE",EDGE,{"disambiguationData":[OSD([sQuery(id+"F0.wireOp",EDGE,"E5.16.5")])],"isStart":true});
            var Q24;
            Q24=makeQuery(id+"F1.opExtrude","CAP_EDGE",EDGE,{"disambiguationData":[OSD([sQuery(id+"F0.wireOp",EDGE,"E5.15.5")])],"isStart":true});
            var Q25;
            Q25=makeQuery(id+"F1.opExtrude","CAP_EDGE",EDGE,{"disambiguationData":[OSD([sQuery(id+"F0.wireOp",EDGE,"E5.14.5")])],"isStart":true});
            var Q26;
            Q26=makeQuery(id+"F1.opExtrude","CAP_EDGE",EDGE,{"disambiguationData":[OSD([sQuery(id+"F0.wireOp",EDGE,"E5.13.5")])],"isStart":true});
            var Q27;
            Q27=makeQuery(id+"F1.opExtrude","CAP_EDGE",EDGE,{"disambiguationData":[OSD([sQuery(id+"F0.wireOp",EDGE,"E5.12.5")])],"isStart":true});
            var Q28;
            Q28=makeQuery(id+"F1.opExtrude","CAP_EDGE",EDGE,{"disambiguationData":[OSD([sQuery(id+"F0.wireOp",EDGE,"E5.11.5")])],"isStart":true});
            var Q29;
            Q29=makeQuery(id+"F1.opExtrude","CAP_EDGE",EDGE,{"disambiguationData":[OSD([sQuery(id+"F0.wireOp",EDGE,"E5.10.5")])],"isStart":true});
            var Q30;
            Q30=makeQuery(id+"F1.opExtrude","CAP_EDGE",EDGE,{"disambiguationData":[OSD([sQuery(id+"F0.wireOp",EDGE,"E5.9.5")])],"isStart":true});
            var Q31;
            Q31=makeQuery(id+"F1.opExtrude","CAP_EDGE",EDGE,{"disambiguationData":[OSD([sQuery(id+"F0.wireOp",EDGE,"E5.8.5")])],"isStart":true});
            var Q32;
            Q32=makeQuery(id+"F1.opExtrude","CAP_EDGE",EDGE,{"disambiguationData":[OSD([sQuery(id+"F0.wireOp",EDGE,"E5.7.5")])],"isStart":true});
            var Q33;
            Q33=makeQuery(id+"F1.opExtrude","CAP_EDGE",EDGE,{"disambiguationData":[OSD([sQuery(id+"F0.wireOp",EDGE,"E5.6.5")])],"isStart":true});
            var Q34;
            Q34=makeQuery(id+"F1.opExtrude","CAP_EDGE",EDGE,{"disambiguationData":[OSD([sQuery(id+"F0.wireOp",EDGE,"E5.5.5")])],"isStart":true});
            var Q35;
            Q35=makeQuery(id+"F1.opExtrude","CAP_EDGE",EDGE,{"disambiguationData":[OSD([sQuery(id+"F0.wireOp",EDGE,"E5.20.5")])],"isStart":true});
            fillet(context, id + "F3", {"entities" : qUnion([Q0, Q1, Q2, Q3, Q4, Q5, Q6, Q7, Q8, Q9, Q10, Q11, Q12, Q13, Q14, Q15, Q16, Q17, Q18, Q19, Q20, Q21, Q22, Q23, Q24, Q25, Q26, Q27, Q28, Q29, Q30, Q31, Q32, Q33, Q34, Q35]), "radius" : 5.08 * mm, "tangentPropagation" : true, "allowEdgeOverflow" : false});
        }
        {
            var Q0;
            Q0=makeQuery(id+"F1.opExtrude","CAP_EDGE",EDGE,{"disambiguationData":[OSD([sQuery(id+"F0.wireOp",EDGE,"E12.trimOffspring")])],"isStart":true});
            var Q1;
            Q1=makeQuery(id+"F1.opExtrude","CAP_EDGE",EDGE,{"disambiguationData":[OSD([sQuery(id+"F0.wireOp",EDGE,"E13.trimOffspring")])],"isStart":true});
            var Q2;
            Q2=makeQuery(id+"F1.opExtrude","CAP_EDGE",EDGE,{"disambiguationData":[OSD([sQuery(id+"F0.wireOp",EDGE,"E14.trimOffspring")])],"isStart":true});
            var Q3;
            Q3=makeQuery(id+"F1.opExtrude","CAP_EDGE",EDGE,{"disambiguationData":[OSD([sQuery(id+"F0.wireOp",EDGE,"E15.trimOffspring")])],"isStart":true});
            var Q4;
            Q4=makeQuery(id+"F1.opExtrude","CAP_EDGE",EDGE,{"disambiguationData":[OSD([sQuery(id+"F0.wireOp",EDGE,"E16.trimOffspring")])],"isStart":true});
            var Q5;
            Q5=makeQuery(id+"F1.opExtrude","CAP_EDGE",EDGE,{"disambiguationData":[OSD([sQuery(id+"F0.wireOp",EDGE,"E17.trimOffspring")])],"isStart":true});
            var Q6;
            Q6=makeQuery(id+"F1.opExtrude","CAP_EDGE",EDGE,{"disambiguationData":[OSD([sQuery(id+"F0.wireOp",EDGE,"E11.trimOffspring")])],"isStart":true});
            var Q7;
            Q7=makeQuery(id+"F1.opExtrude","CAP_EDGE",EDGE,{"disambiguationData":[OSD([sQuery(id+"F0.wireOp",EDGE,"E10.trimOffspring")])],"isStart":true});
            var Q8;
            Q8=makeQuery(id+"F1.opExtrude","CAP_EDGE",EDGE,{"disambiguationData":[OSD([sQuery(id+"F0.wireOp",EDGE,"E0")])],"isStart":true});
            var Q9;
            Q9=makeQuery(id+"F1.opExtrude","CAP_EDGE",EDGE,{"disambiguationData":[OSD([sQuery(id+"F0.wireOp",EDGE,"E6.trimOffspring")])],"isStart":true});
            var Q10;
            Q10=makeQuery(id+"F1.opExtrude","CAP_EDGE",EDGE,{"disambiguationData":[OSD([sQuery(id+"F0.wireOp",EDGE,"E7.trimOffspring")])],"isStart":true});
            var Q11;
            Q11=makeQuery(id+"F1.opExtrude","CAP_EDGE",EDGE,{"disambiguationData":[OSD([sQuery(id+"F0.wireOp",EDGE,"E8.trimOffspring")])],"isStart":true});
            var Q12;
            Q12=makeQuery(id+"F1.opExtrude","CAP_EDGE",EDGE,{"disambiguationData":[OSD([sQuery(id+"F0.wireOp",EDGE,"E9.trimOffspring")])],"isStart":true});
            var Q13;
            Q13=makeQuery(id+"F1.opExtrude","CAP_EDGE",EDGE,{"disambiguationData":[OSD([sQuery(id+"F0.wireOp",EDGE,"E40.trimOffspring")])],"isStart":true});
            var Q14;
            Q14=makeQuery(id+"F1.opExtrude","CAP_EDGE",EDGE,{"disambiguationData":[OSD([sQuery(id+"F0.wireOp",EDGE,"E39.trimOffspring")])],"isStart":true});
            var Q15;
            Q15=makeQuery(id+"F1.opExtrude","CAP_EDGE",EDGE,{"disambiguationData":[OSD([sQuery(id+"F0.wireOp",EDGE,"E38.trimOffspring")])],"isStart":true});
            var Q16;
            Q16=makeQuery(id+"F1.opExtrude","CAP_EDGE",EDGE,{"disambiguationData":[OSD([sQuery(id+"F0.wireOp",EDGE,"E37.trimOffspring")])],"isStart":true});
            var Q17;
            Q17=makeQuery(id+"F1.opExtrude","CAP_EDGE",EDGE,{"disambiguationData":[OSD([sQuery(id+"F0.wireOp",EDGE,"E36.trimOffspring")])],"isStart":true});
            var Q18;
            Q18=makeQuery(id+"F1.opExtrude","CAP_EDGE",EDGE,{"disambiguationData":[OSD([sQuery(id+"F0.wireOp",EDGE,"E35.trimOffspring")])],"isStart":true});
            var Q19;
            Q19=makeQuery(id+"F1.opExtrude","CAP_EDGE",EDGE,{"disambiguationData":[OSD([sQuery(id+"F0.wireOp",EDGE,"E34.trimOffspring")])],"isStart":true});
            var Q20;
            Q20=makeQuery(id+"F1.opExtrude","CAP_EDGE",EDGE,{"disambiguationData":[OSD([sQuery(id+"F0.wireOp",EDGE,"E33.trimOffspring")])],"isStart":true});
            var Q21;
            Q21=makeQuery(id+"F1.opExtrude","CAP_EDGE",EDGE,{"disambiguationData":[OSD([sQuery(id+"F0.wireOp",EDGE,"E32.trimOffspring")])],"isStart":true});
            var Q22;
            Q22=makeQuery(id+"F1.opExtrude","CAP_EDGE",EDGE,{"disambiguationData":[OSD([sQuery(id+"F0.wireOp",EDGE,"E31.trimOffspring")])],"isStart":true});
            var Q23;
            Q23=makeQuery(id+"F1.opExtrude","CAP_EDGE",EDGE,{"disambiguationData":[OSD([sQuery(id+"F0.wireOp",EDGE,"E30.trimOffspring")])],"isStart":true});
            var Q24;
            Q24=makeQuery(id+"F1.opExtrude","CAP_EDGE",EDGE,{"disambiguationData":[OSD([sQuery(id+"F0.wireOp",EDGE,"E28.trimOffspring")])],"isStart":true});
            var Q25;
            Q25=makeQuery(id+"F1.opExtrude","CAP_EDGE",EDGE,{"disambiguationData":[OSD([sQuery(id+"F0.wireOp",EDGE,"E27.trimOffspring")])],"isStart":true});
            var Q26;
            Q26=makeQuery(id+"F1.opExtrude","CAP_EDGE",EDGE,{"disambiguationData":[OSD([sQuery(id+"F0.wireOp",EDGE,"E26.trimOffspring")])],"isStart":true});
            var Q27;
            Q27=makeQuery(id+"F1.opExtrude","CAP_EDGE",EDGE,{"disambiguationData":[OSD([sQuery(id+"F0.wireOp",EDGE,"E25.trimOffspring")])],"isStart":true});
            var Q28;
            Q28=makeQuery(id+"F1.opExtrude","CAP_EDGE",EDGE,{"disambiguationData":[OSD([sQuery(id+"F0.wireOp",EDGE,"E24.trimOffspring")])],"isStart":true});
            var Q29;
            Q29=makeQuery(id+"F1.opExtrude","CAP_EDGE",EDGE,{"disambiguationData":[OSD([sQuery(id+"F0.wireOp",EDGE,"E23.trimOffspring")])],"isStart":true});
            var Q30;
            Q30=makeQuery(id+"F1.opExtrude","CAP_EDGE",EDGE,{"disambiguationData":[OSD([sQuery(id+"F0.wireOp",EDGE,"E22.trimOffspring")])],"isStart":true});
            var Q31;
            Q31=makeQuery(id+"F1.opExtrude","CAP_EDGE",EDGE,{"disambiguationData":[OSD([sQuery(id+"F0.wireOp",EDGE,"E21.trimOffspring")])],"isStart":true});
            var Q32;
            Q32=makeQuery(id+"F1.opExtrude","CAP_EDGE",EDGE,{"disambiguationData":[OSD([sQuery(id+"F0.wireOp",EDGE,"E20.trimOffspring")])],"isStart":true});
            var Q33;
            Q33=makeQuery(id+"F1.opExtrude","CAP_EDGE",EDGE,{"disambiguationData":[OSD([sQuery(id+"F0.wireOp",EDGE,"E19.trimOffspring")])],"isStart":true});
            var Q34;
            Q34=makeQuery(id+"F1.opExtrude","CAP_EDGE",EDGE,{"disambiguationData":[OSD([sQuery(id+"F0.wireOp",EDGE,"E18.trimOffspring")])],"isStart":true});
            var Q35;
            Q35=makeQuery(id+"F1.opExtrude","CAP_EDGE",EDGE,{"disambiguationData":[OSD([sQuery(id+"F0.wireOp",EDGE,"E29.trimOffspring")])],"isStart":true});
            fillet(context, id + "F4", {"entities" : qUnion([Q0, Q1, Q2, Q3, Q4, Q5, Q6, Q7, Q8, Q9, Q10, Q11, Q12, Q13, Q14, Q15, Q16, Q17, Q18, Q19, Q20, Q21, Q22, Q23, Q24, Q25, Q26, Q27, Q28, Q29, Q30, Q31, Q32, Q33, Q34, Q35]), "radius" : 5.08 * mm, "tangentPropagation" : true, "allowEdgeOverflow" : false});
        }
        {
            var Q0;
            Q0=makeQuery(id+"F1.opExtrude","CAP_EDGE",EDGE,{"disambiguationData":[OSD([sQuery(id+"F0.wireOp",EDGE,"E28.trimOffspring")])],"isStart":false});
            var Q1;
            Q1=makeQuery(id+"F1.opExtrude","CAP_EDGE",EDGE,{"disambiguationData":[OSD([sQuery(id+"F0.wireOp",EDGE,"E27.trimOffspring")])],"isStart":false});
            var Q2;
            Q2=makeQuery(id+"F1.opExtrude","CAP_EDGE",EDGE,{"disambiguationData":[OSD([sQuery(id+"F0.wireOp",EDGE,"E26.trimOffspring")])],"isStart":false});
            var Q3;
            Q3=makeQuery(id+"F1.opExtrude","CAP_EDGE",EDGE,{"disambiguationData":[OSD([sQuery(id+"F0.wireOp",EDGE,"E25.trimOffspring")])],"isStart":false});
            var Q4;
            Q4=makeQuery(id+"F1.opExtrude","CAP_EDGE",EDGE,{"disambiguationData":[OSD([sQuery(id+"F0.wireOp",EDGE,"E24.trimOffspring")])],"isStart":false});
            var Q5;
            Q5=makeQuery(id+"F1.opExtrude","CAP_EDGE",EDGE,{"disambiguationData":[OSD([sQuery(id+"F0.wireOp",EDGE,"E23.trimOffspring")])],"isStart":false});
            var Q6;
            Q6=makeQuery(id+"F1.opExtrude","CAP_EDGE",EDGE,{"disambiguationData":[OSD([sQuery(id+"F0.wireOp",EDGE,"E22.trimOffspring")])],"isStart":false});
            var Q7;
            Q7=makeQuery(id+"F1.opExtrude","CAP_EDGE",EDGE,{"disambiguationData":[OSD([sQuery(id+"F0.wireOp",EDGE,"E29.trimOffspring")])],"isStart":false});
            var Q8;
            Q8=makeQuery(id+"F1.opExtrude","CAP_EDGE",EDGE,{"disambiguationData":[OSD([sQuery(id+"F0.wireOp",EDGE,"E30.trimOffspring")])],"isStart":false});
            var Q9;
            Q9=makeQuery(id+"F1.opExtrude","CAP_EDGE",EDGE,{"disambiguationData":[OSD([sQuery(id+"F0.wireOp",EDGE,"E31.trimOffspring")])],"isStart":false});
            var Q10;
            Q10=makeQuery(id+"F1.opExtrude","CAP_EDGE",EDGE,{"disambiguationData":[OSD([sQuery(id+"F0.wireOp",EDGE,"E32.trimOffspring")])],"isStart":false});
            var Q11;
            Q11=makeQuery(id+"F1.opExtrude","CAP_EDGE",EDGE,{"disambiguationData":[OSD([sQuery(id+"F0.wireOp",EDGE,"E33.trimOffspring")])],"isStart":false});
            var Q12;
            Q12=makeQuery(id+"F1.opExtrude","CAP_EDGE",EDGE,{"disambiguationData":[OSD([sQuery(id+"F0.wireOp",EDGE,"E34.trimOffspring")])],"isStart":false});
            var Q13;
            Q13=makeQuery(id+"F1.opExtrude","CAP_EDGE",EDGE,{"disambiguationData":[OSD([sQuery(id+"F0.wireOp",EDGE,"E35.trimOffspring")])],"isStart":false});
            var Q14;
            Q14=makeQuery(id+"F1.opExtrude","CAP_EDGE",EDGE,{"disambiguationData":[OSD([sQuery(id+"F0.wireOp",EDGE,"E36.trimOffspring")])],"isStart":false});
            var Q15;
            Q15=makeQuery(id+"F1.opExtrude","CAP_EDGE",EDGE,{"disambiguationData":[OSD([sQuery(id+"F0.wireOp",EDGE,"E37.trimOffspring")])],"isStart":false});
            var Q16;
            Q16=makeQuery(id+"F1.opExtrude","CAP_EDGE",EDGE,{"disambiguationData":[OSD([sQuery(id+"F0.wireOp",EDGE,"E38.trimOffspring")])],"isStart":false});
            var Q17;
            Q17=makeQuery(id+"F1.opExtrude","CAP_EDGE",EDGE,{"disambiguationData":[OSD([sQuery(id+"F0.wireOp",EDGE,"E39.trimOffspring")])],"isStart":false});
            var Q18;
            Q18=makeQuery(id+"F1.opExtrude","CAP_EDGE",EDGE,{"disambiguationData":[OSD([sQuery(id+"F0.wireOp",EDGE,"E21.trimOffspring")])],"isStart":false});
            var Q19;
            Q19=makeQuery(id+"F1.opExtrude","CAP_EDGE",EDGE,{"disambiguationData":[OSD([sQuery(id+"F0.wireOp",EDGE,"E20.trimOffspring")])],"isStart":false});
            var Q20;
            Q20=makeQuery(id+"F1.opExtrude","CAP_EDGE",EDGE,{"disambiguationData":[OSD([sQuery(id+"F0.wireOp",EDGE,"E19.trimOffspring")])],"isStart":false});
            var Q21;
            Q21=makeQuery(id+"F1.opExtrude","CAP_EDGE",EDGE,{"disambiguationData":[OSD([sQuery(id+"F0.wireOp",EDGE,"E18.trimOffspring")])],"isStart":false});
            var Q22;
            Q22=makeQuery(id+"F1.opExtrude","CAP_EDGE",EDGE,{"disambiguationData":[OSD([sQuery(id+"F0.wireOp",EDGE,"E0")])],"isStart":false});
            var Q23;
            Q23=makeQuery(id+"F1.opExtrude","CAP_EDGE",EDGE,{"disambiguationData":[OSD([sQuery(id+"F0.wireOp",EDGE,"E6.trimOffspring")])],"isStart":false});
            var Q24;
            Q24=makeQuery(id+"F1.opExtrude","CAP_EDGE",EDGE,{"disambiguationData":[OSD([sQuery(id+"F0.wireOp",EDGE,"E7.trimOffspring")])],"isStart":false});
            var Q25;
            Q25=makeQuery(id+"F1.opExtrude","CAP_EDGE",EDGE,{"disambiguationData":[OSD([sQuery(id+"F0.wireOp",EDGE,"E9.trimOffspring")])],"isStart":false});
            var Q26;
            Q26=makeQuery(id+"F1.opExtrude","CAP_EDGE",EDGE,{"disambiguationData":[OSD([sQuery(id+"F0.wireOp",EDGE,"E40.trimOffspring")])],"isStart":false});
            var Q27;
            Q27=makeQuery(id+"F1.opExtrude","CAP_EDGE",EDGE,{"disambiguationData":[OSD([sQuery(id+"F0.wireOp",EDGE,"E17.trimOffspring")])],"isStart":false});
            var Q28;
            Q28=makeQuery(id+"F1.opExtrude","CAP_EDGE",EDGE,{"disambiguationData":[OSD([sQuery(id+"F0.wireOp",EDGE,"E16.trimOffspring")])],"isStart":false});
            var Q29;
            Q29=makeQuery(id+"F1.opExtrude","CAP_EDGE",EDGE,{"disambiguationData":[OSD([sQuery(id+"F0.wireOp",EDGE,"E14.trimOffspring")])],"isStart":false});
            var Q30;
            Q30=makeQuery(id+"F1.opExtrude","CAP_EDGE",EDGE,{"disambiguationData":[OSD([sQuery(id+"F0.wireOp",EDGE,"E13.trimOffspring")])],"isStart":false});
            var Q31;
            Q31=makeQuery(id+"F1.opExtrude","CAP_EDGE",EDGE,{"disambiguationData":[OSD([sQuery(id+"F0.wireOp",EDGE,"E12.trimOffspring")])],"isStart":false});
            var Q32;
            Q32=makeQuery(id+"F1.opExtrude","CAP_EDGE",EDGE,{"disambiguationData":[OSD([sQuery(id+"F0.wireOp",EDGE,"E11.trimOffspring")])],"isStart":false});
            var Q33;
            Q33=makeQuery(id+"F1.opExtrude","CAP_EDGE",EDGE,{"disambiguationData":[OSD([sQuery(id+"F0.wireOp",EDGE,"E10.trimOffspring")])],"isStart":false});
            var Q34;
            Q34=makeQuery(id+"F1.opExtrude","CAP_EDGE",EDGE,{"disambiguationData":[OSD([sQuery(id+"F0.wireOp",EDGE,"E8.trimOffspring")])],"isStart":false});
            var Q35;
            Q35=makeQuery(id+"F1.opExtrude","CAP_EDGE",EDGE,{"disambiguationData":[OSD([sQuery(id+"F0.wireOp",EDGE,"E15.trimOffspring")])],"isStart":false});
            fillet(context, id + "F5", {"entities" : qUnion([Q0, Q1, Q2, Q3, Q4, Q5, Q6, Q7, Q8, Q9, Q10, Q11, Q12, Q13, Q14, Q15, Q16, Q17, Q18, Q19, Q20, Q21, Q22, Q23, Q24, Q25, Q26, Q27, Q28, Q29, Q30, Q31, Q32, Q33, Q34, Q35]), "radius" : 5.08 * mm, "tangentPropagation" : true, "allowEdgeOverflow" : false});
        }
        {
            var Q0;
            Q0=makeQuery(id+"F1.opExtrude","SWEPT_FACE",FACE,{"disambiguationData":[OSD([sQuery(id+"F0.wireOp",EDGE,"E1")])]});
            shell(context, id + "F6", {"entities" : qUnion([Q0]), "thickness" : 2.54 * mm});
        }
        {
            var Q0;
            Q0=qCreatedBy(makeId("Front.planeOp"),FACE);
            var sketch = newSketch(context, id + "F7", { "sketchPlane" : qUnion([Q0])});
            skCircle(sketch, "E41", {"center": v(0, 0) * mm, "radius": 20.4 * mm});
            skSolve(sketch);
        }
        {
            var Q0;
            Q0 = qSketchRegion(id + "F7", true);
            extrude(context, id + "F8", {"entities" : qUnion([Q0]), "depth" : 27.94 * mm, "symmetric" : true});
        }
        {
            var Q0;
            Q0=makeQuery(id+"F1.opExtrude","SWEPT_BODY",BODY,{"disambiguationData":[OSD([sQuery(id+"F0.wireOp",EDGE,"E0"),sQuery(id+"F0.wireOp",EDGE,"E1"),sQuery(id+"F0.wireOp",EDGE,"E2.bottom"),sQuery(id+"F0.wireOp",EDGE,"E2.left"),sQuery(id+"F0.wireOp",EDGE,"E2.right"),sQuery(id+"F0.wireOp",EDGE,"E5.1.3"),sQuery(id+"F0.wireOp",EDGE,"E5.1.4"),sQuery(id+"F0.wireOp",EDGE,"E5.1.5"),sQuery(id+"F0.wireOp",EDGE,"E5.2.3"),sQuery(id+"F0.wireOp",EDGE,"E5.2.4"),sQuery(id+"F0.wireOp",EDGE,"E5.2.5"),sQuery(id+"F0.wireOp",EDGE,"E5.3.3"),sQuery(id+"F0.wireOp",EDGE,"E5.3.4"),sQuery(id+"F0.wireOp",EDGE,"E5.3.5"),sQuery(id+"F0.wireOp",EDGE,"E5.4.3"),sQuery(id+"F0.wireOp",EDGE,"E5.4.4"),sQuery(id+"F0.wireOp",EDGE,"E5.4.5"),sQuery(id+"F0.wireOp",EDGE,"E5.5.3"),sQuery(id+"F0.wireOp",EDGE,"E5.5.4"),sQuery(id+"F0.wireOp",EDGE,"E5.5.5"),sQuery(id+"F0.wireOp",EDGE,"E5.6.3"),sQuery(id+"F0.wireOp",EDGE,"E5.6.4"),sQuery(id+"F0.wireOp",EDGE,"E5.6.5"),sQuery(id+"F0.wireOp",EDGE,"E5.7.3"),sQuery(id+"F0.wireOp",EDGE,"E5.7.4"),sQuery(id+"F0.wireOp",EDGE,"E5.7.5"),sQuery(id+"F0.wireOp",EDGE,"E5.8.3"),sQuery(id+"F0.wireOp",EDGE,"E5.8.4"),sQuery(id+"F0.wireOp",EDGE,"E5.8.5"),sQuery(id+"F0.wireOp",EDGE,"E5.9.3"),sQuery(id+"F0.wireOp",EDGE,"E5.9.4"),sQuery(id+"F0.wireOp",EDGE,"E5.9.5"),sQuery(id+"F0.wireOp",EDGE,"E5.10.3"),sQuery(id+"F0.wireOp",EDGE,"E5.10.4"),sQuery(id+"F0.wireOp",EDGE,"E5.10.5"),sQuery(id+"F0.wireOp",EDGE,"E5.11.3"),sQuery(id+"F0.wireOp",EDGE,"E5.11.4"),sQuery(id+"F0.wireOp",EDGE,"E5.11.5"),sQuery(id+"F0.wireOp",EDGE,"E5.12.3"),sQuery(id+"F0.wireOp",EDGE,"E5.12.4"),sQuery(id+"F0.wireOp",EDGE,"E5.12.5"),sQuery(id+"F0.wireOp",EDGE,"E5.13.3"),sQuery(id+"F0.wireOp",EDGE,"E5.13.4"),sQuery(id+"F0.wireOp",EDGE,"E5.13.5"),sQuery(id+"F0.wireOp",EDGE,"E5.14.3"),sQuery(id+"F0.wireOp",EDGE,"E5.14.4"),sQuery(id+"F0.wireOp",EDGE,"E5.14.5"),sQuery(id+"F0.wireOp",EDGE,"E5.15.3"),sQuery(id+"F0.wireOp",EDGE,"E5.15.4"),sQuery(id+"F0.wireOp",EDGE,"E5.15.5"),sQuery(id+"F0.wireOp",EDGE,"E5.16.3"),sQuery(id+"F0.wireOp",EDGE,"E5.16.4"),sQuery(id+"F0.wireOp",EDGE,"E5.16.5"),sQuery(id+"F0.wireOp",EDGE,"E5.17.3"),sQuery(id+"F0.wireOp",EDGE,"E5.17.4"),sQuery(id+"F0.wireOp",EDGE,"E5.17.5"),sQuery(id+"F0.wireOp",EDGE,"E5.18.3"),sQuery(id+"F0.wireOp",EDGE,"E5.18.4"),sQuery(id+"F0.wireOp",EDGE,"E5.18.5"),sQuery(id+"F0.wireOp",EDGE,"E5.19.3"),sQuery(id+"F0.wireOp",EDGE,"E5.19.4"),sQuery(id+"F0.wireOp",EDGE,"E5.19.5"),sQuery(id+"F0.wireOp",EDGE,"E5.20.3"),sQuery(id+"F0.wireOp",EDGE,"E5.20.4"),sQuery(id+"F0.wireOp",EDGE,"E5.20.5"),sQuery(id+"F0.wireOp",EDGE,"E5.21.3"),sQuery(id+"F0.wireOp",EDGE,"E5.21.4"),sQuery(id+"F0.wireOp",EDGE,"E5.21.5"),sQuery(id+"F0.wireOp",EDGE,"E5.22.3"),sQuery(id+"F0.wireOp",EDGE,"E5.22.4"),sQuery(id+"F0.wireOp",EDGE,"E5.22.5"),sQuery(id+"F0.wireOp",EDGE,"E5.23.3"),sQuery(id+"F0.wireOp",EDGE,"E5.23.4"),sQuery(id+"F0.wireOp",EDGE,"E5.23.5"),sQuery(id+"F0.wireOp",EDGE,"E5.24.3"),sQuery(id+"F0.wireOp",EDGE,"E5.24.4"),sQuery(id+"F0.wireOp",EDGE,"E5.24.5"),sQuery(id+"F0.wireOp",EDGE,"E5.25.3"),sQuery(id+"F0.wireOp",EDGE,"E5.25.4"),sQuery(id+"F0.wireOp",EDGE,"E5.25.5"),sQuery(id+"F0.wireOp",EDGE,"E5.26.3"),sQuery(id+"F0.wireOp",EDGE,"E5.26.4"),sQuery(id+"F0.wireOp",EDGE,"E5.26.5"),sQuery(id+"F0.wireOp",EDGE,"E5.27.3"),sQuery(id+"F0.wireOp",EDGE,"E5.27.4"),sQuery(id+"F0.wireOp",EDGE,"E5.27.5"),sQuery(id+"F0.wireOp",EDGE,"E5.28.3"),sQuery(id+"F0.wireOp",EDGE,"E5.28.4"),sQuery(id+"F0.wireOp",EDGE,"E5.28.5"),sQuery(id+"F0.wireOp",EDGE,"E5.29.3"),sQuery(id+"F0.wireOp",EDGE,"E5.29.4"),sQuery(id+"F0.wireOp",EDGE,"E5.29.5"),sQuery(id+"F0.wireOp",EDGE,"E5.30.3"),sQuery(id+"F0.wireOp",EDGE,"E5.30.4"),sQuery(id+"F0.wireOp",EDGE,"E5.30.5"),sQuery(id+"F0.wireOp",EDGE,"E5.31.3"),sQuery(id+"F0.wireOp",EDGE,"E5.31.4"),sQuery(id+"F0.wireOp",EDGE,"E5.31.5"),sQuery(id+"F0.wireOp",EDGE,"E5.32.3"),sQuery(id+"F0.wireOp",EDGE,"E5.32.4"),sQuery(id+"F0.wireOp",EDGE,"E5.32.5"),sQuery(id+"F0.wireOp",EDGE,"E5.33.3"),sQuery(id+"F0.wireOp",EDGE,"E5.33.4"),sQuery(id+"F0.wireOp",EDGE,"E5.33.5"),sQuery(id+"F0.wireOp",EDGE,"E5.34.3"),sQuery(id+"F0.wireOp",EDGE,"E5.34.4"),sQuery(id+"F0.wireOp",EDGE,"E5.34.5"),sQuery(id+"F0.wireOp",EDGE,"E5.35.3"),sQuery(id+"F0.wireOp",EDGE,"E5.35.4"),sQuery(id+"F0.wireOp",EDGE,"E5.35.5"),sQuery(id+"F0.wireOp",EDGE,"E6.trimOffspring"),sQuery(id+"F0.wireOp",EDGE,"E7.trimOffspring"),sQuery(id+"F0.wireOp",EDGE,"E8.trimOffspring"),sQuery(id+"F0.wireOp",EDGE,"E9.trimOffspring"),sQuery(id+"F0.wireOp",EDGE,"E10.trimOffspring"),sQuery(id+"F0.wireOp",EDGE,"E11.trimOffspring"),sQuery(id+"F0.wireOp",EDGE,"E12.trimOffspring"),sQuery(id+"F0.wireOp",EDGE,"E13.trimOffspring"),sQuery(id+"F0.wireOp",EDGE,"E14.trimOffspring"),sQuery(id+"F0.wireOp",EDGE,"E15.trimOffspring"),sQuery(id+"F0.wireOp",EDGE,"E16.trimOffspring"),sQuery(id+"F0.wireOp",EDGE,"E17.trimOffspring"),sQuery(id+"F0.wireOp",EDGE,"E18.trimOffspring"),sQuery(id+"F0.wireOp",EDGE,"E19.trimOffspring"),sQuery(id+"F0.wireOp",EDGE,"E20.trimOffspring"),sQuery(id+"F0.wireOp",EDGE,"E21.trimOffspring"),sQuery(id+"F0.wireOp",EDGE,"E22.trimOffspring"),sQuery(id+"F0.wireOp",EDGE,"E23.trimOffspring"),sQuery(id+"F0.wireOp",EDGE,"E24.trimOffspring"),sQuery(id+"F0.wireOp",EDGE,"E25.trimOffspring"),sQuery(id+"F0.wireOp",EDGE,"E26.trimOffspring"),sQuery(id+"F0.wireOp",EDGE,"E27.trimOffspring"),sQuery(id+"F0.wireOp",EDGE,"E28.trimOffspring"),sQuery(id+"F0.wireOp",EDGE,"E29.trimOffspring"),sQuery(id+"F0.wireOp",EDGE,"E30.trimOffspring"),sQuery(id+"F0.wireOp",EDGE,"E31.trimOffspring"),sQuery(id+"F0.wireOp",EDGE,"E32.trimOffspring"),sQuery(id+"F0.wireOp",EDGE,"E33.trimOffspring"),sQuery(id+"F0.wireOp",EDGE,"E34.trimOffspring"),sQuery(id+"F0.wireOp",EDGE,"E35.trimOffspring"),sQuery(id+"F0.wireOp",EDGE,"E36.trimOffspring"),sQuery(id+"F0.wireOp",EDGE,"E37.trimOffspring"),sQuery(id+"F0.wireOp",EDGE,"E38.trimOffspring"),sQuery(id+"F0.wireOp",EDGE,"E39.trimOffspring"),sQuery(id+"F0.wireOp",EDGE,"E40.trimOffspring")])]});
            var Q1;
            Q1=makeQuery(id+"F8.opExtrude","SWEPT_BODY",BODY,{"disambiguationData":[OSD([sQuery(id+"F7.wireOp",EDGE,"E41")])]});
            booleanBodies(context, id + "F9", {"operationType" : BooleanOperationType.SUBTRACTION, "tools" : qUnion([Q0]), "targets" : qUnion([Q1]), "keepTools" : true});
        }
        {
            var Q0;
            Q0=makeQuery(id+"F8.opExtrude","SWEPT_BODY",BODY,{"disambiguationData":[OSD([sQuery(id+"F7.wireOp",EDGE,"E41")])]});
            transform(context, id + "F10", {"entities" : qUnion([Q0]), "transformType" : TransformType.TRANSLATION_3D, "dx" : 0 * mm, "dy" : -128.02 * mm, "dz" : 0 * mm, "makeCopy" : false});
        }
        {
            var Q0;
            Q0=makeQuery(id+"F8.opExtrude","CAP_FACE",FACE,{"disambiguationData":[OSD([sQuery(id+"F7.wireOp",EDGE,"E41")])],"isStart":false});
            var sketch = newSketch(context, id + "F11", { "sketchPlane" : qUnion([Q0])});
            skPoint(sketch, "E42", {"position": v(0, 0) * mm});
            skSolve(sketch);
        }
        {
            var Q0;
            Q0=makeQuery(id+"F8.opExtrude","CAP_FACE",FACE,{"disambiguationData":[OSD([sQuery(id+"F7.wireOp",EDGE,"E41")])],"isStart":true});
            var sketch = newSketch(context, id + "F12", { "sketchPlane" : qUnion([Q0])});
            skPoint(sketch, "E43", {"position": v(0, 0) * mm});
            skSolve(sketch);
        }
        {
            var Q0;
            Q0=qCreatedBy(makeId("Right.planeOp"),FACE);
            var sketch = newSketch(context, id + "F13", { "sketchPlane" : qUnion([Q0])});
            skPoint(sketch, "E44.0", {"position": v(-141.99, 0) * mm});
            skPoint(sketch, "E45.0", {"position": v(-114.05, 0) * mm});
            skLineSegment(sketch, "E46", {"start": v(-141.99, 0) * mm, "end": v(-114.05, 0) * mm, "construction": true});
            skLineSegment(sketch, "E47.bottom", {"start": v(-136.9, 20.4) * mm, "end": v(-119.13, 20.4) * mm});
            skLineSegment(sketch, "E47.top", {"start": v(-136.9, 14.06) * mm, "end": v(-119.13, 14.06) * mm});
            skLineSegment(sketch, "E47.left", {"start": v(-136.9, 20.4) * mm, "end": v(-136.9, 14.06) * mm});
            skLineSegment(sketch, "E47.right", {"start": v(-119.13, 20.4) * mm, "end": v(-119.13, 14.06) * mm});
            skLineSegment(sketch, "E48", {"start": v(-138.18, 20.4) * mm, "end": v(-117.86, 20.4) * mm});
            skSolve(sketch);
        }
        {
            var Q0;
            Q0 = qSketchRegion(id + "F13", true);
            var Q1;
            {var subQ0=sQuery(id+"F0.wireOp",EDGE,"E40.trimOffspring");var subQ1=sQuery(id+"F0.wireOp",EDGE,"E39.trimOffspring");var subQ2=sQuery(id+"F0.wireOp",EDGE,"E38.trimOffspring");var subQ3=sQuery(id+"F0.wireOp",EDGE,"E37.trimOffspring");var subQ4=sQuery(id+"F0.wireOp",EDGE,"E36.trimOffspring");var subQ5=sQuery(id+"F0.wireOp",EDGE,"E35.trimOffspring");var subQ6=sQuery(id+"F0.wireOp",EDGE,"E34.trimOffspring");var subQ7=sQuery(id+"F0.wireOp",EDGE,"E33.trimOffspring");var subQ8=sQuery(id+"F0.wireOp",EDGE,"E32.trimOffspring");var subQ9=sQuery(id+"F0.wireOp",EDGE,"E31.trimOffspring");var subQ10=sQuery(id+"F0.wireOp",EDGE,"E30.trimOffspring");var subQ11=sQuery(id+"F0.wireOp",EDGE,"E29.trimOffspring");var subQ12=sQuery(id+"F0.wireOp",EDGE,"E28.trimOffspring");var subQ13=sQuery(id+"F0.wireOp",EDGE,"E27.trimOffspring");var subQ14=sQuery(id+"F0.wireOp",EDGE,"E26.trimOffspring");var subQ15=sQuery(id+"F0.wireOp",EDGE,"E25.trimOffspring");var subQ16=sQuery(id+"F0.wireOp",EDGE,"E24.trimOffspring");var subQ17=sQuery(id+"F0.wireOp",EDGE,"E23.trimOffspring");var subQ18=sQuery(id+"F0.wireOp",EDGE,"E22.trimOffspring");var subQ19=sQuery(id+"F0.wireOp",EDGE,"E21.trimOffspring");var subQ20=sQuery(id+"F0.wireOp",EDGE,"E20.trimOffspring");var subQ21=sQuery(id+"F0.wireOp",EDGE,"E19.trimOffspring");var subQ22=sQuery(id+"F0.wireOp",EDGE,"E18.trimOffspring");var subQ23=sQuery(id+"F0.wireOp",EDGE,"E17.trimOffspring");var subQ24=sQuery(id+"F0.wireOp",EDGE,"E16.trimOffspring");var subQ25=sQuery(id+"F0.wireOp",EDGE,"E15.trimOffspring");var subQ26=sQuery(id+"F0.wireOp",EDGE,"E14.trimOffspring");var subQ27=sQuery(id+"F0.wireOp",EDGE,"E13.trimOffspring");var subQ28=sQuery(id+"F0.wireOp",EDGE,"E12.trimOffspring");var subQ29=sQuery(id+"F0.wireOp",EDGE,"E11.trimOffspring");var subQ30=sQuery(id+"F0.wireOp",EDGE,"E10.trimOffspring");var subQ31=sQuery(id+"F0.wireOp",EDGE,"E9.trimOffspring");var subQ32=sQuery(id+"F0.wireOp",EDGE,"E8.trimOffspring");var subQ33=sQuery(id+"F0.wireOp",EDGE,"E7.trimOffspring");var subQ34=sQuery(id+"F0.wireOp",EDGE,"E6.trimOffspring");var subQ35=sQuery(id+"F0.wireOp",EDGE,"E5.35.5");var subQ36=sQuery(id+"F0.wireOp",EDGE,"E5.35.4");var subQ37=sQuery(id+"F0.wireOp",EDGE,"E5.35.3");var subQ38=sQuery(id+"F0.wireOp",EDGE,"E5.34.5");var subQ39=sQuery(id+"F0.wireOp",EDGE,"E5.34.4");var subQ40=sQuery(id+"F0.wireOp",EDGE,"E5.34.3");var subQ41=sQuery(id+"F0.wireOp",EDGE,"E5.33.5");var subQ42=sQuery(id+"F0.wireOp",EDGE,"E5.33.4");var subQ43=sQuery(id+"F0.wireOp",EDGE,"E5.33.3");var subQ44=sQuery(id+"F0.wireOp",EDGE,"E5.32.5");var subQ45=sQuery(id+"F0.wireOp",EDGE,"E5.32.4");var subQ46=sQuery(id+"F0.wireOp",EDGE,"E5.32.3");var subQ47=sQuery(id+"F0.wireOp",EDGE,"E5.31.5");var subQ48=sQuery(id+"F0.wireOp",EDGE,"E5.31.4");var subQ49=sQuery(id+"F0.wireOp",EDGE,"E5.31.3");var subQ50=sQuery(id+"F0.wireOp",EDGE,"E5.30.5");var subQ51=sQuery(id+"F0.wireOp",EDGE,"E5.30.4");var subQ52=sQuery(id+"F0.wireOp",EDGE,"E5.30.3");var subQ53=sQuery(id+"F0.wireOp",EDGE,"E5.29.5");var subQ54=sQuery(id+"F0.wireOp",EDGE,"E5.29.4");var subQ55=sQuery(id+"F0.wireOp",EDGE,"E5.29.3");var subQ56=sQuery(id+"F0.wireOp",EDGE,"E5.28.5");var subQ57=sQuery(id+"F0.wireOp",EDGE,"E5.28.4");var subQ58=sQuery(id+"F0.wireOp",EDGE,"E5.28.3");var subQ59=sQuery(id+"F0.wireOp",EDGE,"E5.27.5");var subQ60=sQuery(id+"F0.wireOp",EDGE,"E5.27.4");var subQ61=sQuery(id+"F0.wireOp",EDGE,"E5.27.3");var subQ62=sQuery(id+"F0.wireOp",EDGE,"E5.26.5");var subQ63=sQuery(id+"F0.wireOp",EDGE,"E5.26.4");var subQ64=sQuery(id+"F0.wireOp",EDGE,"E5.26.3");var subQ65=sQuery(id+"F0.wireOp",EDGE,"E5.25.5");var subQ66=sQuery(id+"F0.wireOp",EDGE,"E5.25.4");var subQ67=sQuery(id+"F0.wireOp",EDGE,"E5.25.3");var subQ68=sQuery(id+"F0.wireOp",EDGE,"E5.24.5");var subQ69=sQuery(id+"F0.wireOp",EDGE,"E5.24.4");var subQ70=sQuery(id+"F0.wireOp",EDGE,"E5.24.3");var subQ71=sQuery(id+"F0.wireOp",EDGE,"E5.23.5");var subQ72=sQuery(id+"F0.wireOp",EDGE,"E5.23.4");var subQ73=sQuery(id+"F0.wireOp",EDGE,"E5.23.3");var subQ74=sQuery(id+"F0.wireOp",EDGE,"E5.22.5");var subQ75=sQuery(id+"F0.wireOp",EDGE,"E5.22.4");var subQ76=sQuery(id+"F0.wireOp",EDGE,"E5.22.3");var subQ77=sQuery(id+"F0.wireOp",EDGE,"E5.21.5");var subQ78=sQuery(id+"F0.wireOp",EDGE,"E5.21.4");var subQ79=sQuery(id+"F0.wireOp",EDGE,"E5.21.3");var subQ80=sQuery(id+"F0.wireOp",EDGE,"E5.20.5");var subQ81=sQuery(id+"F0.wireOp",EDGE,"E5.20.4");var subQ82=sQuery(id+"F0.wireOp",EDGE,"E5.20.3");var subQ83=sQuery(id+"F0.wireOp",EDGE,"E5.19.5");var subQ84=sQuery(id+"F0.wireOp",EDGE,"E5.19.4");var subQ85=sQuery(id+"F0.wireOp",EDGE,"E5.19.3");var subQ86=sQuery(id+"F0.wireOp",EDGE,"E5.18.5");var subQ87=sQuery(id+"F0.wireOp",EDGE,"E5.18.4");var subQ88=sQuery(id+"F0.wireOp",EDGE,"E5.18.3");var subQ89=sQuery(id+"F0.wireOp",EDGE,"E5.17.5");var subQ90=sQuery(id+"F0.wireOp",EDGE,"E5.17.4");var subQ91=sQuery(id+"F0.wireOp",EDGE,"E5.17.3");var subQ92=sQuery(id+"F0.wireOp",EDGE,"E5.16.5");var subQ93=sQuery(id+"F0.wireOp",EDGE,"E5.16.4");var subQ94=sQuery(id+"F0.wireOp",EDGE,"E5.16.3");var subQ95=sQuery(id+"F0.wireOp",EDGE,"E5.15.5");var subQ96=sQuery(id+"F0.wireOp",EDGE,"E5.15.4");var subQ97=sQuery(id+"F0.wireOp",EDGE,"E5.15.3");var subQ98=sQuery(id+"F0.wireOp",EDGE,"E5.14.5");var subQ99=sQuery(id+"F0.wireOp",EDGE,"E5.14.4");var subQ100=sQuery(id+"F0.wireOp",EDGE,"E5.14.3");var subQ101=sQuery(id+"F0.wireOp",EDGE,"E5.13.5");var subQ102=sQuery(id+"F0.wireOp",EDGE,"E5.13.4");var subQ103=sQuery(id+"F0.wireOp",EDGE,"E5.13.3");var subQ104=sQuery(id+"F0.wireOp",EDGE,"E5.12.5");var subQ105=sQuery(id+"F0.wireOp",EDGE,"E5.12.4");var subQ106=sQuery(id+"F0.wireOp",EDGE,"E5.12.3");var subQ107=sQuery(id+"F0.wireOp",EDGE,"E5.11.5");var subQ108=sQuery(id+"F0.wireOp",EDGE,"E5.11.4");var subQ109=sQuery(id+"F0.wireOp",EDGE,"E5.11.3");var subQ110=sQuery(id+"F0.wireOp",EDGE,"E5.10.5");var subQ111=sQuery(id+"F0.wireOp",EDGE,"E5.10.4");var subQ112=sQuery(id+"F0.wireOp",EDGE,"E5.10.3");var subQ113=sQuery(id+"F0.wireOp",EDGE,"E5.9.5");var subQ114=sQuery(id+"F0.wireOp",EDGE,"E5.9.4");var subQ115=sQuery(id+"F0.wireOp",EDGE,"E5.9.3");var subQ116=sQuery(id+"F0.wireOp",EDGE,"E5.8.5");var subQ117=sQuery(id+"F0.wireOp",EDGE,"E5.8.4");var subQ118=sQuery(id+"F0.wireOp",EDGE,"E5.8.3");var subQ119=sQuery(id+"F0.wireOp",EDGE,"E5.7.5");var subQ120=sQuery(id+"F0.wireOp",EDGE,"E5.7.4");var subQ121=sQuery(id+"F0.wireOp",EDGE,"E5.7.3");var subQ122=sQuery(id+"F0.wireOp",EDGE,"E5.6.5");var subQ123=sQuery(id+"F0.wireOp",EDGE,"E5.6.4");var subQ124=sQuery(id+"F0.wireOp",EDGE,"E5.6.3");var subQ125=sQuery(id+"F0.wireOp",EDGE,"E5.5.5");var subQ126=sQuery(id+"F0.wireOp",EDGE,"E5.5.4");var subQ127=sQuery(id+"F0.wireOp",EDGE,"E5.5.3");var subQ128=sQuery(id+"F0.wireOp",EDGE,"E5.4.5");var subQ129=sQuery(id+"F0.wireOp",EDGE,"E5.4.4");var subQ130=sQuery(id+"F0.wireOp",EDGE,"E5.4.3");var subQ131=sQuery(id+"F0.wireOp",EDGE,"E5.3.5");var subQ132=sQuery(id+"F0.wireOp",EDGE,"E5.3.4");var subQ133=sQuery(id+"F0.wireOp",EDGE,"E5.3.3");var subQ134=sQuery(id+"F0.wireOp",EDGE,"E5.2.5");var subQ135=sQuery(id+"F0.wireOp",EDGE,"E5.2.4");var subQ136=sQuery(id+"F0.wireOp",EDGE,"E5.2.3");var subQ137=sQuery(id+"F0.wireOp",EDGE,"E5.1.5");var subQ138=sQuery(id+"F0.wireOp",EDGE,"E5.1.4");var subQ139=sQuery(id+"F0.wireOp",EDGE,"E5.1.3");var subQ140=sQuery(id+"F0.wireOp",EDGE,"E2.right");var subQ141=sQuery(id+"F0.wireOp",EDGE,"E2.left");var subQ142=sQuery(id+"F0.wireOp",EDGE,"E2.bottom");var subQ143=sQuery(id+"F0.wireOp",EDGE,"E1");var subQ144=sQuery(id+"F0.wireOp",EDGE,"E0");Q1=makeQuery(id+"F9.opBoolean","SPLIT",FACE,{"disambiguationData":[TD([makeQuery(id+"F6.opShell","OFFSET_FACE",FACE,{"disambiguationData":[OSD([subQ144,subQ143,subQ142,subQ141,subQ140,subQ139,subQ138,subQ137,subQ136,subQ135,subQ134,subQ133,subQ132,subQ131,subQ130,subQ129,subQ128,subQ127,subQ126,subQ125,subQ124,subQ123,subQ122,subQ121,subQ120,subQ119,subQ118,subQ117,subQ116,subQ115,subQ114,subQ113,subQ112,subQ111,subQ110,subQ109,subQ108,subQ107,subQ106,subQ105,subQ104,subQ103,subQ102,subQ101,subQ100,subQ99,subQ98,subQ97,subQ96,subQ95,subQ94,subQ93,subQ92,subQ91,subQ90,subQ89,subQ88,subQ87,subQ86,subQ85,subQ84,subQ83,subQ82,subQ81,subQ80,subQ79,subQ78,subQ77,subQ76,subQ75,subQ74,subQ73,subQ72,subQ71,subQ70,subQ69,subQ68,subQ67,subQ66,subQ65,subQ64,subQ63,subQ62,subQ61,subQ60,subQ59,subQ58,subQ57,subQ56,subQ55,subQ54,subQ53,subQ52,subQ51,subQ50,subQ49,subQ48,subQ47,subQ46,subQ45,subQ44,subQ43,subQ42,subQ41,subQ40,subQ39,subQ38,subQ37,subQ36,subQ35,subQ34,subQ33,subQ32,subQ31,subQ30,subQ29,subQ28,subQ27,subQ26,subQ25,subQ24,subQ23,subQ22,subQ21,subQ20,subQ19,subQ18,subQ17,subQ16,subQ15,subQ14,subQ13,subQ12,subQ11,subQ10,subQ9,subQ8,subQ7,subQ6,subQ5,subQ4,subQ3,subQ2,subQ1,subQ0]),TDD([makeQuery(id+"F1.opExtrude","CAP_FACE",FACE,{"disambiguationData":[OSD([subQ144,subQ143,subQ142,subQ141,subQ140,subQ139,subQ138,subQ137,subQ136,subQ135,subQ134,subQ133,subQ132,subQ131,subQ130,subQ129,subQ128,subQ127,subQ126,subQ125,subQ124,subQ123,subQ122,subQ121,subQ120,subQ119,subQ118,subQ117,subQ116,subQ115,subQ114,subQ113,subQ112,subQ111,subQ110,subQ109,subQ108,subQ107,subQ106,subQ105,subQ104,subQ103,subQ102,subQ101,subQ100,subQ99,subQ98,subQ97,subQ96,subQ95,subQ94,subQ93,subQ92,subQ91,subQ90,subQ89,subQ88,subQ87,subQ86,subQ85,subQ84,subQ83,subQ82,subQ81,subQ80,subQ79,subQ78,subQ77,subQ76,subQ75,subQ74,subQ73,subQ72,subQ71,subQ70,subQ69,subQ68,subQ67,subQ66,subQ65,subQ64,subQ63,subQ62,subQ61,subQ60,subQ59,subQ58,subQ57,subQ56,subQ55,subQ54,subQ53,subQ52,subQ51,subQ50,subQ49,subQ48,subQ47,subQ46,subQ45,subQ44,subQ43,subQ42,subQ41,subQ40,subQ39,subQ38,subQ37,subQ36,subQ35,subQ34,subQ33,subQ32,subQ31,subQ30,subQ29,subQ28,subQ27,subQ26,subQ25,subQ24,subQ23,subQ22,subQ21,subQ20,subQ19,subQ18,subQ17,subQ16,subQ15,subQ14,subQ13,subQ12,subQ11,subQ10,subQ9,subQ8,subQ7,subQ6,subQ5,subQ4,subQ3,subQ2,subQ1,subQ0])],"isStart":true})])]})])],"derivedFrom":makeQuery(id+"F8.opExtrude","SWEPT_FACE",FACE,{"disambiguationData":[OSD([sQuery(id+"F7.wireOp",EDGE,"E41")])]})});}
            revolve(context, id + "F14", {"operationType" : NewBodyOperationType.REMOVE, "entities" : qUnion([Q0]), "axis" : qUnion([Q1]), "revolveType" : RevolveType.FULL, "oppositeDirection" : true});
        }
        {
            var Q0;
            Q0=makeQuery(id+"F14.boolean.opBoolean","COPY",EDGE,{"derivedFrom":makeQuery(id+"F14.opRevolve","SWEPT_EDGE",EDGE,{"disambiguationData":[OSD([sQuery(id+"F13.wireOp",EDGE,"E47.top"),sQuery(id+"F13.wireOp",EDGE,"E47.right")])]})});
            var Q1;
            Q1=makeQuery(id+"F14.boolean.opBoolean","COPY",EDGE,{"derivedFrom":makeQuery(id+"F14.opRevolve","SWEPT_EDGE",EDGE,{"disambiguationData":[OSD([sQuery(id+"F13.wireOp",EDGE,"E47.top"),sQuery(id+"F13.wireOp",EDGE,"E47.left")])]})});
            fillet(context, id + "F15", {"entities" : qUnion([Q0, Q1]), "radius" : 5.08 * mm, "tangentPropagation" : true, "allowEdgeOverflow" : false});
        }
        {
            var Q0;
            Q0=makeQuery(id+"F8.opExtrude","CAP_FACE",FACE,{"disambiguationData":[OSD([sQuery(id+"F7.wireOp",EDGE,"E41")])],"isStart":false});
            var Q1;
            Q1=makeQuery(id+"F8.opExtrude","CAP_FACE",FACE,{"disambiguationData":[OSD([sQuery(id+"F7.wireOp",EDGE,"E41")])],"isStart":true});
            shell(context, id + "F16", {"entities" : qUnion([Q0, Q1]), "thickness" : 2.54 * mm});
        }
        {
            var Q0;
            Q0=qCreatedBy(makeId("Right.planeOp"),FACE);
            var sketch = newSketch(context, id + "F17", { "sketchPlane" : qUnion([Q0])});
            skPoint(sketch, "E49.0", {"position": v(-141.99, 0) * mm});
            skPoint(sketch, "E50.0", {"position": v(-114.05, 0) * mm});
            skLineSegment(sketch, "E51", {"start": v(-141.99, 0) * mm, "end": v(-129.29, 0) * mm, "construction": true});
            skLineSegment(sketch, "E52.bottom", {"start": v(-129.29, 0) * mm, "end": v(-126.75, 0) * mm});
            skLineSegment(sketch, "E52.top", {"start": v(-129.29, 12.18) * mm, "end": v(-126.75, 12.18) * mm});
            skLineSegment(sketch, "E52.left", {"start": v(-129.29, 1.74) * mm, "end": v(-129.29, 12.18) * mm});
            skLineSegment(sketch, "E52.right", {"start": v(-126.75, 1.74) * mm, "end": v(-126.75, 12.18) * mm});
            skLineSegment(sketch, "E53", {"start": v(-129.29, 1.74) * mm, "end": v(-126.75, 1.74) * mm});
            skLineSegment(sketch, "E54.trimOffspring", {"start": v(-126.75, 0) * mm, "end": v(-114.05, 0) * mm, "construction": true});
            skSolve(sketch);
        }
        {
            var Q0;
            Q0 = qSketchRegion(id + "F17", true);
            var Q1;
            Q1=sQuery(id+"F17.wireOp",EDGE,"E51");
            revolve(context, id + "F18", {"operationType" : NewBodyOperationType.ADD, "entities" : qUnion([Q0]), "axis" : qUnion([Q1]), "revolveType" : RevolveType.FULL});
        }
        {
            var Q0;
            Q0=makeQuery(id+"F18.boolean.opBoolean","INTERSECT",EDGE,{"derivedFrom":[makeQuery(id+"F16.opShell","OFFSET_FACE",FACE,{"disambiguationData":[OSD([sQuery(id+"F13.wireOp",EDGE,"E47.top")])]}),makeQuery(id+"F18.opRevolve","SWEPT_FACE",FACE,{"disambiguationData":[OSD([sQuery(id+"F17.wireOp",EDGE,"E52.left")])]})]});
            var Q1;
            Q1=makeQuery(id+"F18.boolean.opBoolean","INTERSECT",EDGE,{"derivedFrom":[makeQuery(id+"F16.opShell","OFFSET_FACE",FACE,{"disambiguationData":[OSD([sQuery(id+"F13.wireOp",EDGE,"E47.top")])]}),makeQuery(id+"F18.opRevolve","SWEPT_FACE",FACE,{"disambiguationData":[OSD([sQuery(id+"F17.wireOp",EDGE,"E52.right")])]})]});
            fillet(context, id + "F19", {"entities" : qUnion([Q0, Q1]), "radius" : 5.08 * mm, "tangentPropagation" : true, "allowEdgeOverflow" : false});
        }
        {
            var Q0;
            Q0=makeQuery(id+"F14.boolean.opBoolean","COPY",FACE,{"derivedFrom":makeQuery(id+"F14.opRevolve","SWEPT_FACE",FACE,{"disambiguationData":[OSD([sQuery(id+"F13.wireOp",EDGE,"E47.top")])]})});
            var Q1;
            Q1=makeQuery(id+"F15.opFillet","BLEND_FACE",FACE,{"disambiguationData":[OSD([sQuery(id+"F13.wireOp",EDGE,"E47.top"),sQuery(id+"F13.wireOp",EDGE,"E47.right")])]});
            var Q2;
            Q2=makeQuery(id+"F15.opFillet","BLEND_FACE",FACE,{"disambiguationData":[OSD([sQuery(id+"F13.wireOp",EDGE,"E47.top"),sQuery(id+"F13.wireOp",EDGE,"E47.left")])]});
            shell(context, id + "F20", {"entities" : qUnion([Q0, Q1, Q2]), "thickness" : 2.03 * mm});
        }
    });
